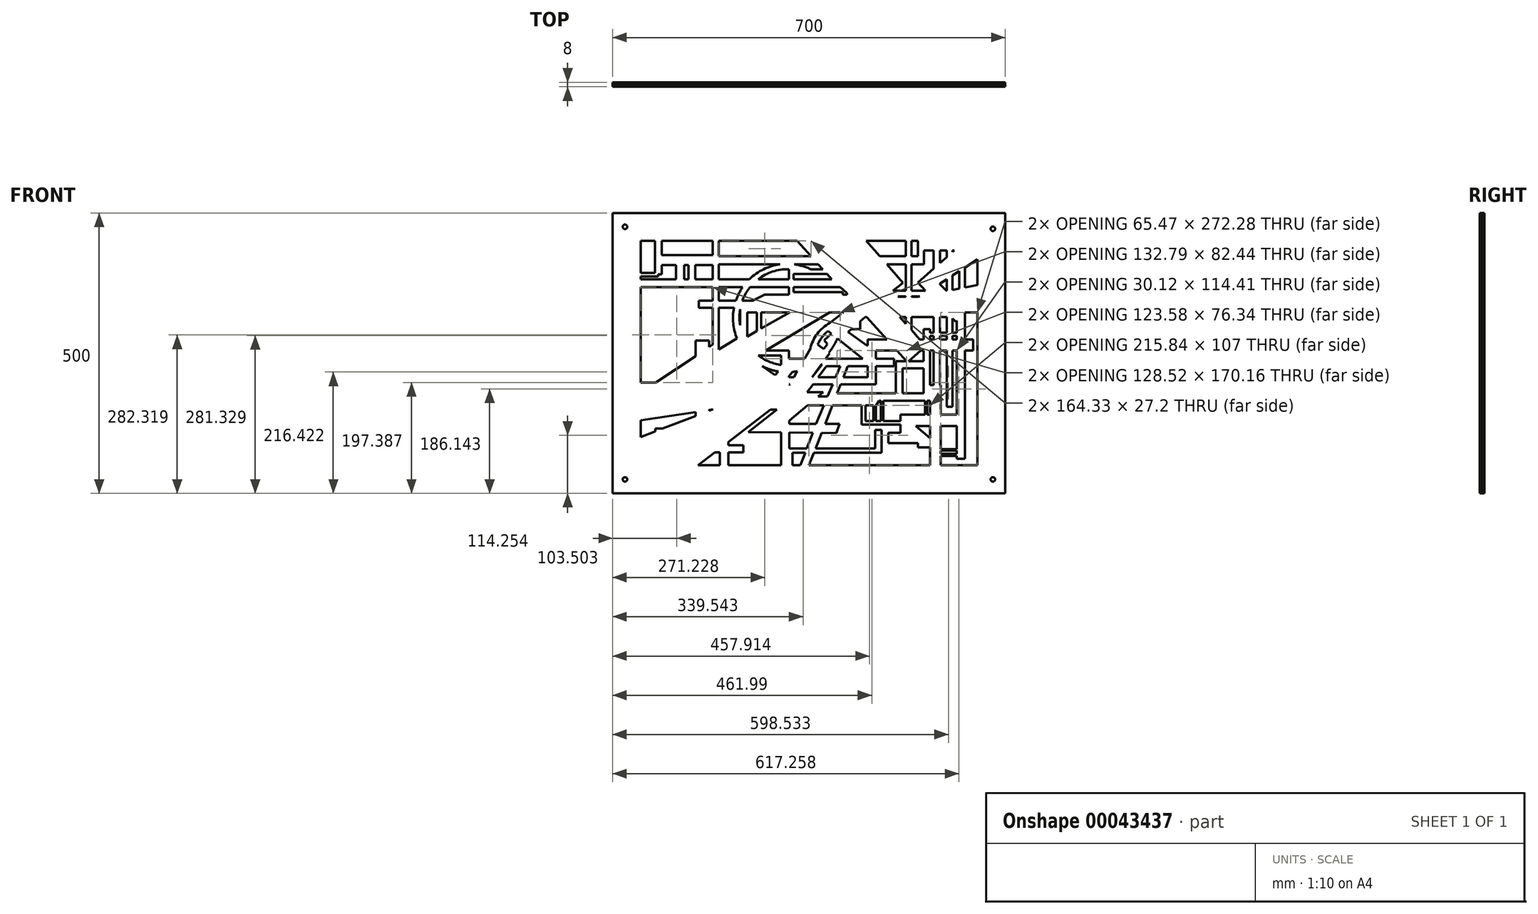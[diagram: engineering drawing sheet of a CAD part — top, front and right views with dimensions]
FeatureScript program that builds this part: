
annotation { "Feature Type Name" : "Feature", "Feature Type Description" : "" }
export const myFeature = defineFeature(function(context is Context, id is Id, definition is map)
    precondition{}
    {
        {
            var Q0;
            Q0=qCreatedBy(makeId("Front.planeOp"),FACE);
            var sketch = newSketch(context, id + "F0", { "sketchPlane" : qUnion([Q0])});
            skLineSegment(sketch, "E0.bottom", {"start": v(-405.94, 245.41) * mm, "end": v(294.06, 245.41) * mm});
            skLineSegment(sketch, "E0.top", {"start": v(-405.94, -254.59) * mm, "end": v(294.06, -254.59) * mm});
            skLineSegment(sketch, "E0.left", {"start": v(-405.94, 245.41) * mm, "end": v(-405.94, -254.59) * mm});
            skLineSegment(sketch, "E0.right", {"start": v(294.06, 245.41) * mm, "end": v(294.06, -254.59) * mm});
            skLineSegment(sketch, "E1.bottom", {"start": v(-355.94, 195.41) * mm, "end": v(-55.94, 195.41) * mm});
            skLineSegment(sketch, "E1.top", {"start": v(-355.94, -204.59) * mm, "end": v(244.06, -204.59) * mm});
            skLineSegment(sketch, "E1.left", {"start": v(-355.94, 195.41) * mm, "end": v(-355.94, -204.59) * mm});
            skLineSegment(sketch, "E1.right", {"start": v(244.06, 195.41) * mm, "end": v(244.06, -204.59) * mm});
            skLineSegment(sketch, "E2", {"start": v(231.3, 195.41) * mm, "end": v(150.42, 122.81) * mm});
            skLineSegment(sketch, "E3", {"start": v(150.42, 122.81) * mm, "end": v(157.7, 114.7) * mm});
            skLineSegment(sketch, "E4", {"start": v(167.3, 121.13) * mm, "end": v(244.06, 172.52) * mm});
            skLineSegment(sketch, "E5", {"start": v(244.06, 172.52) * mm, "end": v(244.06, 195.41) * mm});
            skLineSegment(sketch, "E6", {"start": v(150.42, 122.81) * mm, "end": v(179.6, 90.3) * mm});
            skLineSegment(sketch, "E7", {"start": v(205.45, 61.5) * mm, "end": v(213.96, 69.15) * mm});
            skLineSegment(sketch, "E8", {"start": v(213.96, 69.15) * mm, "end": v(204.55, 79.64) * mm});
            skLineSegment(sketch, "E9", {"start": v(-355.94, -176.1) * mm, "end": v(-156.42, -87.52) * mm});
            skLineSegment(sketch, "E10", {"start": v(-131.37, -87.52) * mm, "end": v(-322.83, -204.59) * mm});
            skLineSegment(sketch, "E11", {"start": v(-322.83, -204.59) * mm, "end": v(-355.94, -204.59) * mm});
            skLineSegment(sketch, "E12", {"start": v(-55.94, 195.41) * mm, "end": v(39.07, 90.3) * mm});
            skLineSegment(sketch, "E13", {"start": v(108.4, 13.58) * mm, "end": v(115.46, 19.96) * mm});
            skLineSegment(sketch, "E14", {"start": v(115.46, 19.96) * mm, "end": v(61.52, 79.64) * mm});
            skLineSegment(sketch, "E15.trimOffspring", {"start": v(-43.13, 195.41) * mm, "end": v(-15.39, 195.41) * mm});
            skLineSegment(sketch, "E16", {"start": v(-15.39, 195.41) * mm, "end": v(66.72, 104.57) * mm});
            skLineSegment(sketch, "E17", {"start": v(95.32, 90.3) * mm, "end": v(96.17, 91.06) * mm});
            skLineSegment(sketch, "E18", {"start": v(96.17, 91.06) * mm, "end": v(83, 105.63) * mm});
            skLineSegment(sketch, "E19", {"start": v(21.81, 195.41) * mm, "end": v(87.2, 123.08) * mm});
            skLineSegment(sketch, "E20", {"start": v(93.99, 115.56) * mm, "end": v(102.37, 123.13) * mm});
            skLineSegment(sketch, "E21", {"start": v(102.37, 123.13) * mm, "end": v(37.03, 195.41) * mm});
            skLineSegment(sketch, "E22", {"start": v(93.99, 115.56) * mm, "end": v(83, 105.63) * mm});
            skLineSegment(sketch, "E23", {"start": v(-21.98, 10.73) * mm, "end": v(-28.78, 18.25) * mm});
            skLineSegment(sketch, "E24", {"start": v(-28.78, 18.25) * mm, "end": v(39.14, 79.64) * mm});
            skLineSegment(sketch, "E25.trimOffspring", {"start": v(76.2, 113.14) * mm, "end": v(1.85, 195.41) * mm});
            skLineSegment(sketch, "E26.trimOffspring", {"start": v(76.2, 113.14) * mm, "end": v(87.2, 123.08) * mm});
            skLineSegment(sketch, "E27.trimOffspring", {"start": v(73.52, 97.05) * mm, "end": v(66.04, 90.3) * mm});
            skLineSegment(sketch, "E28.trimOffspring", {"start": v(73.52, 97.05) * mm, "end": v(79.63, 90.3) * mm});
            skLineSegment(sketch, "E29.trimOffspring", {"start": v(51.45, 90.77) * mm, "end": v(-43.13, 195.41) * mm});
            skLineSegment(sketch, "E30.trimOffspring", {"start": v(51.2, 76.88) * mm, "end": v(-21.98, 10.73) * mm});
            skLineSegment(sketch, "E31.trimOffspring", {"start": v(51.45, 90.77) * mm, "end": v(66.72, 104.57) * mm});
            skLineSegment(sketch, "E32.trimOffspring", {"start": v(51.2, 76.88) * mm, "end": v(108.4, 13.58) * mm});
            skLineSegment(sketch, "E33.trimOffspring", {"start": v(1.85, 195.41) * mm, "end": v(21.81, 195.41) * mm});
            skLineSegment(sketch, "E34.trimOffspring", {"start": v(37.03, 195.41) * mm, "end": v(244.06, 195.41) * mm});
            skLineSegment(sketch, "E35", {"start": v(244.06, 79.64) * mm, "end": v(204.55, 79.64) * mm});
            skLineSegment(sketch, "E36", {"start": v(-158.13, 79.64) * mm, "end": v(-133.99, 90.3) * mm});
            skLineSegment(sketch, "E37", {"start": v(-133.99, 90.3) * mm, "end": v(39.07, 90.3) * mm});
            skLineSegment(sketch, "E38", {"start": v(244.06, 90.3) * mm, "end": v(244.06, 79.64) * mm});
            skLineSegment(sketch, "E39.trimOffspring", {"start": v(95.32, 90.3) * mm, "end": v(179.6, 90.3) * mm});
            skLineSegment(sketch, "E40.trimOffspring", {"start": v(194.99, 90.3) * mm, "end": v(167.3, 121.13) * mm});
            skLineSegment(sketch, "E41.trimOffspring", {"start": v(194.99, 90.3) * mm, "end": v(244.06, 90.3) * mm});
            skLineSegment(sketch, "E42.trimOffspring", {"start": v(189.17, 79.64) * mm, "end": v(205.45, 61.5) * mm});
            skLineSegment(sketch, "E43.trimOffspring", {"start": v(189.17, 79.64) * mm, "end": v(61.52, 79.64) * mm});
            skLineSegment(sketch, "E44.trimOffspring", {"start": v(66.04, 90.3) * mm, "end": v(79.63, 90.3) * mm});
            skLineSegment(sketch, "E45.trimOffspring", {"start": v(39.14, 79.64) * mm, "end": v(-19.56, 79.64) * mm});
            skLineSegment(sketch, "E46", {"start": v(-325.73, -79.87) * mm, "end": v(-46.1, 79.64) * mm});
            skLineSegment(sketch, "E47", {"start": v(-19.56, 79.64) * mm, "end": v(-169.55, -12.55) * mm});
            skLineSegment(sketch, "E48", {"start": v(-257.48, -66.6) * mm, "end": v(-115.3, -66.6) * mm});
            skLineSegment(sketch, "E49", {"start": v(-115.3, -66.6) * mm, "end": v(-185.8, -22.54) * mm});
            skLineSegment(sketch, "E50", {"start": v(-169.55, -12.55) * mm, "end": v(-89.7, -67.55) * mm});
            skLineSegment(sketch, "E51", {"start": v(-89.7, -67.55) * mm, "end": v(-43.18, 0) * mm});
            skLineSegment(sketch, "E52", {"start": v(-43.18, 0) * mm, "end": v(-33.39, -6.75) * mm});
            skLineSegment(sketch, "E53", {"start": v(-33.39, -6.75) * mm, "end": v(-82.64, -78.26) * mm});
            skLineSegment(sketch, "E54", {"start": v(-82.64, -78.26) * mm, "end": v(-131.37, -87.52) * mm});
            skLineSegment(sketch, "E55.trimOffspring", {"start": v(-185.8, -22.54) * mm, "end": v(-257.48, -66.6) * mm});
            skLineSegment(sketch, "E56.trimOffspring", {"start": v(-46.1, 79.64) * mm, "end": v(-158.13, 79.64) * mm});
            skLineSegment(sketch, "E57", {"start": v(-156.42, -87.52) * mm, "end": v(-325.73, -79.87) * mm});
            skCircle(sketch, "E58", {"center": v(-383.92, 220.59) * mm, "radius": 4 * mm});
            skCircle(sketch, "E59", {"center": v(-383.92, -229.76) * mm, "radius": 4 * mm});
            skCircle(sketch, "E60", {"center": v(271.85, -229.76) * mm, "radius": 4 * mm});
            skCircle(sketch, "E61", {"center": v(271.85, 217.02) * mm, "radius": 4 * mm});
            skLineSegment(sketch, "E62", {"start": v(37.03, 195.41) * mm, "end": v(-69.9, 195.41) * mm});
            skSolve(sketch);
        }
        {
            var Q0;
            Q0=makeQuery(id+"F0.imprint","IMPRINT",FACE,{"disambiguationData":[TD([[makeQuery(id+"F0.imprint","IMPRINT",EDGE,{"derivedFrom":sQuery(id+"F0.wireOp",EDGE,"E0.bottom")}),-1.0]])]});
            extrude(context, id + "F1", {"entities" : qUnion([Q0]), "depth" : 4 * mm});
        }
        {
            var Q0;
            Q0=makeQuery(id+"F1.opExtrude","SWEPT_BODY",BODY,{"disambiguationData":[OSD([sQuery(id+"F0.wireOp",EDGE,"E0.bottom"),sQuery(id+"F0.wireOp",EDGE,"E0.top"),sQuery(id+"F0.wireOp",EDGE,"E0.left"),sQuery(id+"F0.wireOp",EDGE,"E0.right"),sQuery(id+"F0.wireOp",EDGE,"E1.bottom"),sQuery(id+"F0.wireOp",EDGE,"E1.top"),sQuery(id+"F0.wireOp",EDGE,"E1.left"),sQuery(id+"F0.wireOp",EDGE,"E1.right"),sQuery(id+"F0.wireOp",EDGE,"E5"),sQuery(id+"F0.wireOp",EDGE,"E11"),sQuery(id+"F0.wireOp",EDGE,"E34.trimOffspring"),sQuery(id+"F0.wireOp",EDGE,"E38"),sQuery(id+"F0.wireOp",EDGE,"E58"),sQuery(id+"F0.wireOp",EDGE,"E59"),sQuery(id+"F0.wireOp",EDGE,"E60"),sQuery(id+"F0.wireOp",EDGE,"E61"),sQuery(id+"F0.wireOp",EDGE,"E62")])]});
            transform(context, id + "F2", {"entities" : qUnion([Q0]), "transformType" : TransformType.COPY});
        }
        {
            var Q0;
            Q0=makeQuery(id+"F1.opExtrude","SWEPT_BODY",BODY,{"disambiguationData":[OSD([sQuery(id+"F0.wireOp",EDGE,"E0.bottom"),sQuery(id+"F0.wireOp",EDGE,"E0.top"),sQuery(id+"F0.wireOp",EDGE,"E0.left"),sQuery(id+"F0.wireOp",EDGE,"E0.right"),sQuery(id+"F0.wireOp",EDGE,"E1.bottom"),sQuery(id+"F0.wireOp",EDGE,"E1.top"),sQuery(id+"F0.wireOp",EDGE,"E1.left"),sQuery(id+"F0.wireOp",EDGE,"E1.right"),sQuery(id+"F0.wireOp",EDGE,"E5"),sQuery(id+"F0.wireOp",EDGE,"E11"),sQuery(id+"F0.wireOp",EDGE,"E34.trimOffspring"),sQuery(id+"F0.wireOp",EDGE,"E38"),sQuery(id+"F0.wireOp",EDGE,"E58"),sQuery(id+"F0.wireOp",EDGE,"E59"),sQuery(id+"F0.wireOp",EDGE,"E60"),sQuery(id+"F0.wireOp",EDGE,"E61"),sQuery(id+"F0.wireOp",EDGE,"E62")])]});
            transform(context, id + "F3", {"entities" : qUnion([Q0]), "transformType" : TransformType.COPY});
        }
        {
            var Q0;
            Q0=makeQuery(id+"F1.opExtrude","SWEPT_BODY",BODY,{"disambiguationData":[OSD([sQuery(id+"F0.wireOp",EDGE,"E0.bottom"),sQuery(id+"F0.wireOp",EDGE,"E0.top"),sQuery(id+"F0.wireOp",EDGE,"E0.left"),sQuery(id+"F0.wireOp",EDGE,"E0.right"),sQuery(id+"F0.wireOp",EDGE,"E1.bottom"),sQuery(id+"F0.wireOp",EDGE,"E1.top"),sQuery(id+"F0.wireOp",EDGE,"E1.left"),sQuery(id+"F0.wireOp",EDGE,"E1.right"),sQuery(id+"F0.wireOp",EDGE,"E5"),sQuery(id+"F0.wireOp",EDGE,"E11"),sQuery(id+"F0.wireOp",EDGE,"E34.trimOffspring"),sQuery(id+"F0.wireOp",EDGE,"E38"),sQuery(id+"F0.wireOp",EDGE,"E58"),sQuery(id+"F0.wireOp",EDGE,"E59"),sQuery(id+"F0.wireOp",EDGE,"E60"),sQuery(id+"F0.wireOp",EDGE,"E61"),sQuery(id+"F0.wireOp",EDGE,"E62")])]});
            transform(context, id + "F4", {"entities" : qUnion([Q0]), "transformType" : TransformType.COPY});
        }
        {
            var Q0;
            Q0=makeQuery(id+"F1.opExtrude","SWEPT_BODY",BODY,{"disambiguationData":[OSD([sQuery(id+"F0.wireOp",EDGE,"E0.bottom"),sQuery(id+"F0.wireOp",EDGE,"E0.top"),sQuery(id+"F0.wireOp",EDGE,"E0.left"),sQuery(id+"F0.wireOp",EDGE,"E0.right"),sQuery(id+"F0.wireOp",EDGE,"E1.bottom"),sQuery(id+"F0.wireOp",EDGE,"E1.top"),sQuery(id+"F0.wireOp",EDGE,"E1.left"),sQuery(id+"F0.wireOp",EDGE,"E1.right"),sQuery(id+"F0.wireOp",EDGE,"E5"),sQuery(id+"F0.wireOp",EDGE,"E11"),sQuery(id+"F0.wireOp",EDGE,"E34.trimOffspring"),sQuery(id+"F0.wireOp",EDGE,"E38"),sQuery(id+"F0.wireOp",EDGE,"E58"),sQuery(id+"F0.wireOp",EDGE,"E59"),sQuery(id+"F0.wireOp",EDGE,"E60"),sQuery(id+"F0.wireOp",EDGE,"E61"),sQuery(id+"F0.wireOp",EDGE,"E62")])]});
            transform(context, id + "F5", {"entities" : qUnion([Q0]), "transformType" : TransformType.COPY});
        }
        {
            var Q0;
            Q0=makeQuery(id+"F1.opExtrude","SWEPT_BODY",BODY,{"disambiguationData":[OSD([sQuery(id+"F0.wireOp",EDGE,"E0.bottom"),sQuery(id+"F0.wireOp",EDGE,"E0.top"),sQuery(id+"F0.wireOp",EDGE,"E0.left"),sQuery(id+"F0.wireOp",EDGE,"E0.right"),sQuery(id+"F0.wireOp",EDGE,"E1.bottom"),sQuery(id+"F0.wireOp",EDGE,"E1.top"),sQuery(id+"F0.wireOp",EDGE,"E1.left"),sQuery(id+"F0.wireOp",EDGE,"E1.right"),sQuery(id+"F0.wireOp",EDGE,"E5"),sQuery(id+"F0.wireOp",EDGE,"E11"),sQuery(id+"F0.wireOp",EDGE,"E34.trimOffspring"),sQuery(id+"F0.wireOp",EDGE,"E38"),sQuery(id+"F0.wireOp",EDGE,"E58"),sQuery(id+"F0.wireOp",EDGE,"E59"),sQuery(id+"F0.wireOp",EDGE,"E60"),sQuery(id+"F0.wireOp",EDGE,"E61"),sQuery(id+"F0.wireOp",EDGE,"E62")])]});
            transform(context, id + "F6", {"entities" : qUnion([Q0]), "transformType" : TransformType.COPY});
        }
        {
            var Q0;
            Q0=makeQuery(id+"F1.opExtrude","SWEPT_BODY",BODY,{"disambiguationData":[OSD([sQuery(id+"F0.wireOp",EDGE,"E0.bottom"),sQuery(id+"F0.wireOp",EDGE,"E0.top"),sQuery(id+"F0.wireOp",EDGE,"E0.left"),sQuery(id+"F0.wireOp",EDGE,"E0.right"),sQuery(id+"F0.wireOp",EDGE,"E1.bottom"),sQuery(id+"F0.wireOp",EDGE,"E1.top"),sQuery(id+"F0.wireOp",EDGE,"E1.left"),sQuery(id+"F0.wireOp",EDGE,"E1.right"),sQuery(id+"F0.wireOp",EDGE,"E5"),sQuery(id+"F0.wireOp",EDGE,"E11"),sQuery(id+"F0.wireOp",EDGE,"E34.trimOffspring"),sQuery(id+"F0.wireOp",EDGE,"E38"),sQuery(id+"F0.wireOp",EDGE,"E58"),sQuery(id+"F0.wireOp",EDGE,"E59"),sQuery(id+"F0.wireOp",EDGE,"E60"),sQuery(id+"F0.wireOp",EDGE,"E61"),sQuery(id+"F0.wireOp",EDGE,"E62")])]});
            transform(context, id + "F7", {"entities" : qUnion([Q0]), "transformType" : TransformType.COPY});
        }
        {
            var Q0;
            Q0=makeQuery(id+"F1.opExtrude","SWEPT_BODY",BODY,{"disambiguationData":[OSD([sQuery(id+"F0.wireOp",EDGE,"E0.bottom"),sQuery(id+"F0.wireOp",EDGE,"E0.top"),sQuery(id+"F0.wireOp",EDGE,"E0.left"),sQuery(id+"F0.wireOp",EDGE,"E0.right"),sQuery(id+"F0.wireOp",EDGE,"E1.bottom"),sQuery(id+"F0.wireOp",EDGE,"E1.top"),sQuery(id+"F0.wireOp",EDGE,"E1.left"),sQuery(id+"F0.wireOp",EDGE,"E1.right"),sQuery(id+"F0.wireOp",EDGE,"E5"),sQuery(id+"F0.wireOp",EDGE,"E11"),sQuery(id+"F0.wireOp",EDGE,"E34.trimOffspring"),sQuery(id+"F0.wireOp",EDGE,"E38"),sQuery(id+"F0.wireOp",EDGE,"E58"),sQuery(id+"F0.wireOp",EDGE,"E59"),sQuery(id+"F0.wireOp",EDGE,"E60"),sQuery(id+"F0.wireOp",EDGE,"E61"),sQuery(id+"F0.wireOp",EDGE,"E62")])]});
            transform(context, id + "F8", {"entities" : qUnion([Q0]), "transformType" : TransformType.COPY});
        }
        {
            var Q0;
            Q0=makeQuery(id+"F1.opExtrude","SWEPT_BODY",BODY,{"disambiguationData":[OSD([sQuery(id+"F0.wireOp",EDGE,"E0.bottom"),sQuery(id+"F0.wireOp",EDGE,"E0.top"),sQuery(id+"F0.wireOp",EDGE,"E0.left"),sQuery(id+"F0.wireOp",EDGE,"E0.right"),sQuery(id+"F0.wireOp",EDGE,"E1.bottom"),sQuery(id+"F0.wireOp",EDGE,"E1.top"),sQuery(id+"F0.wireOp",EDGE,"E1.left"),sQuery(id+"F0.wireOp",EDGE,"E1.right"),sQuery(id+"F0.wireOp",EDGE,"E5"),sQuery(id+"F0.wireOp",EDGE,"E11"),sQuery(id+"F0.wireOp",EDGE,"E34.trimOffspring"),sQuery(id+"F0.wireOp",EDGE,"E38"),sQuery(id+"F0.wireOp",EDGE,"E58"),sQuery(id+"F0.wireOp",EDGE,"E59"),sQuery(id+"F0.wireOp",EDGE,"E60"),sQuery(id+"F0.wireOp",EDGE,"E61"),sQuery(id+"F0.wireOp",EDGE,"E62")])]});
            transform(context, id + "F9", {"entities" : qUnion([Q0]), "transformType" : TransformType.COPY});
        }
        {
            var Q0;
            Q0=makeQuery(id+"F1.opExtrude","SWEPT_BODY",BODY,{"disambiguationData":[OSD([sQuery(id+"F0.wireOp",EDGE,"E0.bottom"),sQuery(id+"F0.wireOp",EDGE,"E0.top"),sQuery(id+"F0.wireOp",EDGE,"E0.left"),sQuery(id+"F0.wireOp",EDGE,"E0.right"),sQuery(id+"F0.wireOp",EDGE,"E1.bottom"),sQuery(id+"F0.wireOp",EDGE,"E1.top"),sQuery(id+"F0.wireOp",EDGE,"E1.left"),sQuery(id+"F0.wireOp",EDGE,"E1.right"),sQuery(id+"F0.wireOp",EDGE,"E5"),sQuery(id+"F0.wireOp",EDGE,"E11"),sQuery(id+"F0.wireOp",EDGE,"E34.trimOffspring"),sQuery(id+"F0.wireOp",EDGE,"E38"),sQuery(id+"F0.wireOp",EDGE,"E58"),sQuery(id+"F0.wireOp",EDGE,"E59"),sQuery(id+"F0.wireOp",EDGE,"E60"),sQuery(id+"F0.wireOp",EDGE,"E61"),sQuery(id+"F0.wireOp",EDGE,"E62")])]});
            transform(context, id + "F10", {"entities" : qUnion([Q0]), "transformType" : TransformType.COPY});
        }
        {
            var Q0;
            Q0=makeQuery(id+"F1.opExtrude","SWEPT_BODY",BODY,{"disambiguationData":[OSD([sQuery(id+"F0.wireOp",EDGE,"E0.bottom"),sQuery(id+"F0.wireOp",EDGE,"E0.top"),sQuery(id+"F0.wireOp",EDGE,"E0.left"),sQuery(id+"F0.wireOp",EDGE,"E0.right"),sQuery(id+"F0.wireOp",EDGE,"E1.bottom"),sQuery(id+"F0.wireOp",EDGE,"E1.top"),sQuery(id+"F0.wireOp",EDGE,"E1.left"),sQuery(id+"F0.wireOp",EDGE,"E1.right"),sQuery(id+"F0.wireOp",EDGE,"E5"),sQuery(id+"F0.wireOp",EDGE,"E11"),sQuery(id+"F0.wireOp",EDGE,"E34.trimOffspring"),sQuery(id+"F0.wireOp",EDGE,"E38"),sQuery(id+"F0.wireOp",EDGE,"E58"),sQuery(id+"F0.wireOp",EDGE,"E59"),sQuery(id+"F0.wireOp",EDGE,"E60"),sQuery(id+"F0.wireOp",EDGE,"E61"),sQuery(id+"F0.wireOp",EDGE,"E62")])]});
            transform(context, id + "F11", {"entities" : qUnion([Q0]), "transformType" : TransformType.COPY});
        }
        {
            var Q0;
            Q0=makeQuery(id+"F1.opExtrude","SWEPT_BODY",BODY,{"disambiguationData":[OSD([sQuery(id+"F0.wireOp",EDGE,"E0.bottom"),sQuery(id+"F0.wireOp",EDGE,"E0.top"),sQuery(id+"F0.wireOp",EDGE,"E0.left"),sQuery(id+"F0.wireOp",EDGE,"E0.right"),sQuery(id+"F0.wireOp",EDGE,"E1.bottom"),sQuery(id+"F0.wireOp",EDGE,"E1.top"),sQuery(id+"F0.wireOp",EDGE,"E1.left"),sQuery(id+"F0.wireOp",EDGE,"E1.right"),sQuery(id+"F0.wireOp",EDGE,"E5"),sQuery(id+"F0.wireOp",EDGE,"E11"),sQuery(id+"F0.wireOp",EDGE,"E34.trimOffspring"),sQuery(id+"F0.wireOp",EDGE,"E38"),sQuery(id+"F0.wireOp",EDGE,"E58"),sQuery(id+"F0.wireOp",EDGE,"E59"),sQuery(id+"F0.wireOp",EDGE,"E60"),sQuery(id+"F0.wireOp",EDGE,"E61"),sQuery(id+"F0.wireOp",EDGE,"E62")])]});
            transform(context, id + "F12", {"entities" : qUnion([Q0]), "transformType" : TransformType.COPY});
        }
        {
            var Q0;
            Q0=makeQuery(id+"F1.opExtrude","SWEPT_BODY",BODY,{"disambiguationData":[OSD([sQuery(id+"F0.wireOp",EDGE,"E0.bottom"),sQuery(id+"F0.wireOp",EDGE,"E0.top"),sQuery(id+"F0.wireOp",EDGE,"E0.left"),sQuery(id+"F0.wireOp",EDGE,"E0.right"),sQuery(id+"F0.wireOp",EDGE,"E1.bottom"),sQuery(id+"F0.wireOp",EDGE,"E1.top"),sQuery(id+"F0.wireOp",EDGE,"E1.left"),sQuery(id+"F0.wireOp",EDGE,"E1.right"),sQuery(id+"F0.wireOp",EDGE,"E5"),sQuery(id+"F0.wireOp",EDGE,"E11"),sQuery(id+"F0.wireOp",EDGE,"E34.trimOffspring"),sQuery(id+"F0.wireOp",EDGE,"E38"),sQuery(id+"F0.wireOp",EDGE,"E58"),sQuery(id+"F0.wireOp",EDGE,"E59"),sQuery(id+"F0.wireOp",EDGE,"E60"),sQuery(id+"F0.wireOp",EDGE,"E61"),sQuery(id+"F0.wireOp",EDGE,"E62")])]});
            transform(context, id + "F13", {"entities" : qUnion([Q0]), "transformType" : TransformType.COPY});
        }
        {
            var Q0;
            Q0=makeQuery(id+"F1.opExtrude","SWEPT_BODY",BODY,{"disambiguationData":[OSD([sQuery(id+"F0.wireOp",EDGE,"E0.bottom"),sQuery(id+"F0.wireOp",EDGE,"E0.top"),sQuery(id+"F0.wireOp",EDGE,"E0.left"),sQuery(id+"F0.wireOp",EDGE,"E0.right"),sQuery(id+"F0.wireOp",EDGE,"E1.bottom"),sQuery(id+"F0.wireOp",EDGE,"E1.top"),sQuery(id+"F0.wireOp",EDGE,"E1.left"),sQuery(id+"F0.wireOp",EDGE,"E1.right"),sQuery(id+"F0.wireOp",EDGE,"E5"),sQuery(id+"F0.wireOp",EDGE,"E11"),sQuery(id+"F0.wireOp",EDGE,"E34.trimOffspring"),sQuery(id+"F0.wireOp",EDGE,"E38"),sQuery(id+"F0.wireOp",EDGE,"E58"),sQuery(id+"F0.wireOp",EDGE,"E59"),sQuery(id+"F0.wireOp",EDGE,"E60"),sQuery(id+"F0.wireOp",EDGE,"E61"),sQuery(id+"F0.wireOp",EDGE,"E62")])]});
            transform(context, id + "F14", {"entities" : qUnion([Q0]), "transformType" : TransformType.COPY});
        }
        {
            var Q0;
            Q0=makeQuery(id+"F1.opExtrude","SWEPT_BODY",BODY,{"disambiguationData":[OSD([sQuery(id+"F0.wireOp",EDGE,"E0.bottom"),sQuery(id+"F0.wireOp",EDGE,"E0.top"),sQuery(id+"F0.wireOp",EDGE,"E0.left"),sQuery(id+"F0.wireOp",EDGE,"E0.right"),sQuery(id+"F0.wireOp",EDGE,"E1.bottom"),sQuery(id+"F0.wireOp",EDGE,"E1.top"),sQuery(id+"F0.wireOp",EDGE,"E1.left"),sQuery(id+"F0.wireOp",EDGE,"E1.right"),sQuery(id+"F0.wireOp",EDGE,"E5"),sQuery(id+"F0.wireOp",EDGE,"E11"),sQuery(id+"F0.wireOp",EDGE,"E34.trimOffspring"),sQuery(id+"F0.wireOp",EDGE,"E38"),sQuery(id+"F0.wireOp",EDGE,"E58"),sQuery(id+"F0.wireOp",EDGE,"E59"),sQuery(id+"F0.wireOp",EDGE,"E60"),sQuery(id+"F0.wireOp",EDGE,"E61"),sQuery(id+"F0.wireOp",EDGE,"E62")])]});
            transform(context, id + "F15", {"entities" : qUnion([Q0]), "transformType" : TransformType.COPY});
        }
        {
            var Q0;
            {var subQ13=sQuery(id+"F0.wireOp",EDGE,"E2");Q0=makeQuery(id+"F0.imprint","IMPRINT",FACE,{"disambiguationData":[TD([[makeQuery(id+"F0.imprint","IMPRINT",EDGE,{"derivedFrom":subQ13}),1.0]])]});}
            extrude(context, id + "F16", {"entities" : qUnion([Q0]), "operationType" : NewBodyOperationType.ADD, "depth" : 4 * mm});
        }
        {
            var Q0;
            Q0=qCreatedBy(makeId("Front.planeOp"),FACE);
            var sketch = newSketch(context, id + "F17", { "sketchPlane" : qUnion([Q0])});
            skLineSegment(sketch, "E63.0", {"start": v(-355.94, 195.41) * mm, "end": v(-55.94, 195.41) * mm});
            skLineSegment(sketch, "E63.1", {"start": v(-355.94, 195.41) * mm, "end": v(-355.94, -204.59) * mm});
            skLineSegment(sketch, "E63.2", {"start": v(-43.13, 195.41) * mm, "end": v(-15.39, 195.41) * mm});
            skLineSegment(sketch, "E63.3", {"start": v(37.03, 195.41) * mm, "end": v(-69.9, 195.41) * mm});
            skLineSegment(sketch, "E63.4", {"start": v(37.03, 195.41) * mm, "end": v(244.06, 195.41) * mm});
            skLineSegment(sketch, "E63.5", {"start": v(244.06, 195.41) * mm, "end": v(244.06, -204.59) * mm});
            skLineSegment(sketch, "E63.6", {"start": v(-355.94, -204.59) * mm, "end": v(244.06, -204.59) * mm});
            skLineSegment(sketch, "E64", {"start": v(-63.2, 195.41) * mm, "end": v(30.8, 93.92) * mm});
            skLineSegment(sketch, "E65", {"start": v(30.8, 93.92) * mm, "end": v(-136.04, 93.92) * mm});
            skLineSegment(sketch, "E66", {"start": v(-136.04, 93.92) * mm, "end": v(-172.77, 76.49) * mm});
            skLineSegment(sketch, "E67", {"start": v(-172.77, 76.49) * mm, "end": v(-59.47, 76.49) * mm});
            skLineSegment(sketch, "E68", {"start": v(-59.47, 76.49) * mm, "end": v(-332.14, -74.16) * mm});
            skLineSegment(sketch, "E69", {"start": v(-332.14, -74.16) * mm, "end": v(-355.94, -74.16) * mm});
            skLineSegment(sketch, "E70", {"start": v(-355.94, -90.97) * mm, "end": v(-180.24, -90.97) * mm});
            skLineSegment(sketch, "E71", {"start": v(-180.24, -90.97) * mm, "end": v(-355.94, -165.05) * mm});
            skLineSegment(sketch, "E72", {"start": v(-355.94, -165.05) * mm, "end": v(-355.94, -204.59) * mm});
            skLineSegment(sketch, "E73", {"start": v(-355.94, -204.59) * mm, "end": v(-294.17, -204.59) * mm});
            skLineSegment(sketch, "E74", {"start": v(-294.17, -204.59) * mm, "end": v(-131.06, -97.2) * mm});
            skLineSegment(sketch, "E75", {"start": v(-131.06, -97.2) * mm, "end": v(-75.04, -86) * mm});
            skLineSegment(sketch, "E76", {"start": v(-75.04, -86) * mm, "end": v(-143.52, -134.55) * mm});
            skLineSegment(sketch, "E77", {"start": v(-143.52, -134.55) * mm, "end": v(-111.77, -134.55) * mm});
            skLineSegment(sketch, "E78", {"start": v(-111.77, -134.55) * mm, "end": v(-47.65, -78.52) * mm});
            skLineSegment(sketch, "E79", {"start": v(-47.65, -78.52) * mm, "end": v(-73.8, -78.52) * mm});
            skLineSegment(sketch, "E80", {"start": v(-73.8, -78.52) * mm, "end": v(-19, -5.06) * mm});
            skLineSegment(sketch, "E81", {"start": v(-19, -5.06) * mm, "end": v(-38.88, 9.75) * mm});
            skLineSegment(sketch, "E82", {"start": v(-38.88, 9.75) * mm, "end": v(-46.4, 16.1) * mm});
            skLineSegment(sketch, "E83", {"start": v(-46.4, 16.1) * mm, "end": v(-90.6, -61.1) * mm});
            skLineSegment(sketch, "E84", {"start": v(-90.6, -61.1) * mm, "end": v(-157.83, -15.02) * mm});
            skLineSegment(sketch, "E85", {"start": v(-157.83, -15.02) * mm, "end": v(-14.65, 70.89) * mm});
            skLineSegment(sketch, "E86", {"start": v(-14.65, 70.89) * mm, "end": v(22.08, 70.89) * mm});
            skLineSegment(sketch, "E87", {"start": v(22.08, 70.89) * mm, "end": v(-19, 39.76) * mm});
            skLineSegment(sketch, "E88", {"start": v(-19, 39.76) * mm, "end": v(39.5, -6.3) * mm});
            skLineSegment(sketch, "E89", {"start": v(39.5, -6.3) * mm, "end": v(44.47, 0) * mm});
            skLineSegment(sketch, "E90", {"start": v(44.47, 0) * mm, "end": v(0, 35.01) * mm});
            skLineSegment(sketch, "E91", {"start": v(0, 35.01) * mm, "end": v(43.24, 74) * mm});
            skLineSegment(sketch, "E92", {"start": v(43.24, 74) * mm, "end": v(109.96, 0) * mm});
            skLineSegment(sketch, "E93", {"start": v(109.96, 0) * mm, "end": v(129.48, 17.6) * mm});
            skLineSegment(sketch, "E94", {"start": v(129.48, 17.6) * mm, "end": v(78.52, 74.13) * mm});
            skLineSegment(sketch, "E95", {"start": v(78.52, 74.13) * mm, "end": v(183.31, 74.13) * mm});
            skLineSegment(sketch, "E96", {"start": v(183.31, 74.13) * mm, "end": v(205.72, 51.59) * mm});
            skLineSegment(sketch, "E97", {"start": v(205.72, 51.59) * mm, "end": v(224.77, 70.52) * mm});
            skLineSegment(sketch, "E98", {"start": v(224.77, 70.52) * mm, "end": v(218.5, 76.81) * mm});
            skLineSegment(sketch, "E99", {"start": v(218.5, 76.81) * mm, "end": v(244.06, 76.81) * mm});
            skLineSegment(sketch, "E100", {"start": v(244.06, 76.81) * mm, "end": v(244.06, 95.79) * mm});
            skLineSegment(sketch, "E101", {"start": v(244.06, 95.79) * mm, "end": v(200.12, 95.79) * mm});
            skLineSegment(sketch, "E102", {"start": v(200.12, 95.79) * mm, "end": v(177.09, 118.82) * mm});
            skLineSegment(sketch, "E103", {"start": v(177.09, 118.82) * mm, "end": v(244.06, 162.4) * mm});
            skLineSegment(sketch, "E104", {"start": v(244.06, 162.4) * mm, "end": v(244.06, 195.41) * mm});
            skLineSegment(sketch, "E105", {"start": v(221.91, 195.41) * mm, "end": v(138.5, 121.31) * mm});
            skLineSegment(sketch, "E106", {"start": v(138.5, 121.31) * mm, "end": v(160.98, 96) * mm});
            skLineSegment(sketch, "E107", {"start": v(160.98, 96) * mm, "end": v(103.63, 96) * mm});
            skLineSegment(sketch, "E108", {"start": v(103.63, 96) * mm, "end": v(92.42, 105.75) * mm});
            skLineSegment(sketch, "E109", {"start": v(92.42, 105.75) * mm, "end": v(111.72, 120.69) * mm});
            skLineSegment(sketch, "E110", {"start": v(111.72, 120.69) * mm, "end": v(46.36, 195.41) * mm});
            skLineSegment(sketch, "E111", {"start": v(46.36, 195.41) * mm, "end": v(-63.2, 195.41) * mm});
            skSolve(sketch);
        }
        {
            var Q0;
            {var subQ3=sQuery(id+"F17.wireOp",EDGE,"E64");Q0=makeQuery(id+"F17.imprint","IMPRINT",FACE,{"disambiguationData":[TD([[makeQuery(id+"F17.imprint","IMPRINT",EDGE,{"derivedFrom":subQ3}),1.0]])]});}
            var Q1;
            Q1=makeQuery(id+"F2.opPattern","COPY",FACE,{"derivedFrom":makeQuery(id+"F1.opExtrude","CAP_FACE",FACE,{"disambiguationData":[OSD([sQuery(id+"F0.wireOp",EDGE,"E0.bottom"),sQuery(id+"F0.wireOp",EDGE,"E0.top"),sQuery(id+"F0.wireOp",EDGE,"E0.left"),sQuery(id+"F0.wireOp",EDGE,"E0.right"),sQuery(id+"F0.wireOp",EDGE,"E1.bottom"),sQuery(id+"F0.wireOp",EDGE,"E1.top"),sQuery(id+"F0.wireOp",EDGE,"E1.left"),sQuery(id+"F0.wireOp",EDGE,"E1.right"),sQuery(id+"F0.wireOp",EDGE,"E5"),sQuery(id+"F0.wireOp",EDGE,"E11"),sQuery(id+"F0.wireOp",EDGE,"E34.trimOffspring"),sQuery(id+"F0.wireOp",EDGE,"E38"),sQuery(id+"F0.wireOp",EDGE,"E58"),sQuery(id+"F0.wireOp",EDGE,"E59"),sQuery(id+"F0.wireOp",EDGE,"E60"),sQuery(id+"F0.wireOp",EDGE,"E61"),sQuery(id+"F0.wireOp",EDGE,"E62")])],"isStart":true}),"instanceName":"1"});
            extrude(context, id + "F18", {"entities" : qUnion([Q0, Q1]), "operationType" : NewBodyOperationType.ADD, "depth" : 4 * mm});
        }
        {
            var Q0;
            Q0=qCreatedBy(makeId("Front.planeOp"),FACE);
            var sketch = newSketch(context, id + "F19", { "sketchPlane" : qUnion([Q0])});
            skLineSegment(sketch, "E112.0", {"start": v(-355.94, 195.41) * mm, "end": v(244.06, 195.41) * mm});
            skLineSegment(sketch, "E112.1", {"start": v(-355.94, 195.41) * mm, "end": v(-355.94, -204.59) * mm});
            skLineSegment(sketch, "E112.2", {"start": v(244.06, -204.59) * mm, "end": v(244.06, 195.41) * mm});
            skLineSegment(sketch, "E112.3", {"start": v(-355.94, -204.59) * mm, "end": v(244.06, -204.59) * mm});
            skLineSegment(sketch, "E113", {"start": v(-77.05, 195.41) * mm, "end": v(-15.71, 127.32) * mm});
            skLineSegment(sketch, "E114", {"start": v(-355.94, 127.32) * mm, "end": v(-15.71, 127.32) * mm});
            skLineSegment(sketch, "E115", {"start": v(-355.94, 127.32) * mm, "end": v(-355.94, 112.81) * mm});
            skLineSegment(sketch, "E116", {"start": v(-355.94, 112.81) * mm, "end": v(0, 112.81) * mm});
            skLineSegment(sketch, "E117", {"start": v(0, 112.81) * mm, "end": v(14.63, 99.62) * mm});
            skLineSegment(sketch, "E118", {"start": v(14.63, 99.62) * mm, "end": v(-135.1, 99.62) * mm});
            skLineSegment(sketch, "E119", {"start": v(-135.1, 99.62) * mm, "end": v(-178.62, 77.85) * mm});
            skLineSegment(sketch, "E120", {"start": v(-178.62, 77.85) * mm, "end": v(-178.62, 25.1) * mm});
            skLineSegment(sketch, "E121", {"start": v(-166.09, 25.1) * mm, "end": v(-166.09, 67.96) * mm});
            skLineSegment(sketch, "E122", {"start": v(-166.09, 67.96) * mm, "end": v(-90.24, 67.96) * mm});
            skLineSegment(sketch, "E123", {"start": v(-90.24, 67.96) * mm, "end": v(-166.09, 25.1) * mm});
            skLineSegment(sketch, "E124", {"start": v(-178.62, 25.1) * mm, "end": v(-328.34, -65.27) * mm});
            skLineSegment(sketch, "E125", {"start": v(-328.34, -65.27) * mm, "end": v(-355.94, -65.27) * mm});
            skLineSegment(sketch, "E126", {"start": v(-355.94, -65.27) * mm, "end": v(-355.94, -104.18) * mm});
            skLineSegment(sketch, "E127", {"start": v(-355.94, -104.18) * mm, "end": v(-203.02, -95.6) * mm});
            skLineSegment(sketch, "E128", {"start": v(-203.02, -95.6) * mm, "end": v(-355.94, -154.3) * mm});
            skLineSegment(sketch, "E129", {"start": v(-355.94, -154.3) * mm, "end": v(-355.94, -204.59) * mm});
            skLineSegment(sketch, "E130", {"start": v(-279.53, -204.59) * mm, "end": v(-132.45, -105.5) * mm});
            skLineSegment(sketch, "E131", {"start": v(-132.45, -105.5) * mm, "end": v(-113.33, -105.5) * mm});
            skLineSegment(sketch, "E132", {"start": v(-113.33, -105.5) * mm, "end": v(-164.11, -145.07) * mm});
            skLineSegment(sketch, "E133", {"start": v(-164.11, -145.07) * mm, "end": v(-49.38, -146.52) * mm});
            skLineSegment(sketch, "E134", {"start": v(-7.14, -147.05) * mm, "end": v(-1.2, -130.56) * mm});
            skLineSegment(sketch, "E135", {"start": v(-1.2, -130.56) * mm, "end": v(-26.97, -130.56) * mm});
            skLineSegment(sketch, "E136", {"start": v(-97.5, -130.56) * mm, "end": v(-30.88, -74.5) * mm});
            skLineSegment(sketch, "E137", {"start": v(-30.88, -74.5) * mm, "end": v(-59.24, -74.5) * mm});
            skLineSegment(sketch, "E138", {"start": v(-59.24, -74.5) * mm, "end": v(-24.95, -27.67) * mm});
            skLineSegment(sketch, "E139", {"start": v(-24.95, -27.67) * mm, "end": v(0, -27.67) * mm});
            skLineSegment(sketch, "E140", {"start": v(0, -27.67) * mm, "end": v(-43.41, -130.56) * mm});
            skLineSegment(sketch, "E141", {"start": v(-49.38, -146.52) * mm, "end": v(-71.11, -204.59) * mm});
            skLineSegment(sketch, "E142", {"start": v(-71.11, -204.59) * mm, "end": v(-55.94, -204.59) * mm});
            skLineSegment(sketch, "E143", {"start": v(-55.94, -204.59) * mm, "end": v(-33.3, -146.72) * mm});
            skLineSegment(sketch, "E144", {"start": v(13.3, -27.67) * mm, "end": v(95.75, -27.67) * mm});
            skLineSegment(sketch, "E145", {"start": v(95.75, -27.67) * mm, "end": v(95.75, -14.48) * mm});
            skLineSegment(sketch, "E146", {"start": v(95.75, -14.48) * mm, "end": v(57.5, -14.48) * mm});
            skLineSegment(sketch, "E147", {"start": v(19.24, -14.48) * mm, "end": v(-15.71, -14.48) * mm});
            skLineSegment(sketch, "E148", {"start": v(-15.71, -14.48) * mm, "end": v(-100.13, -14.48) * mm});
            skLineSegment(sketch, "E149", {"start": v(-100.13, -14.48) * mm, "end": v(-100.13, -25.04) * mm});
            skLineSegment(sketch, "E150", {"start": v(-100.13, -25.04) * mm, "end": v(-32.86, -25.04) * mm});
            skLineSegment(sketch, "E151", {"start": v(-32.86, -25.04) * mm, "end": v(-84.3, -90.99) * mm});
            skLineSegment(sketch, "E152", {"start": v(-84.3, -90.99) * mm, "end": v(-131.13, -90.99) * mm});
            skLineSegment(sketch, "E153", {"start": v(-131.13, -90.99) * mm, "end": v(-73.75, -25.04) * mm});
            skLineSegment(sketch, "E154", {"start": v(-100.13, -25.04) * mm, "end": v(-147.42, -79.38) * mm});
            skLineSegment(sketch, "E155", {"start": v(-147.42, -79.38) * mm, "end": v(-307.9, -79.38) * mm});
            skLineSegment(sketch, "E156", {"start": v(-307.9, -79.38) * mm, "end": v(-52.65, 67.96) * mm});
            skLineSegment(sketch, "E157", {"start": v(-52.65, 67.96) * mm, "end": v(5.4, 67.96) * mm});
            skLineSegment(sketch, "E158", {"start": v(5.4, 67.96) * mm, "end": v(-29.56, 40.92) * mm});
            skLineSegment(sketch, "E159", {"start": v(-29.56, 40.92) * mm, "end": v(39.69, -14.48) * mm});
            skLineSegment(sketch, "E160", {"start": v(57.5, -14.48) * mm, "end": v(57.5, 0) * mm});
            skLineSegment(sketch, "E161", {"start": v(57.5, 0) * mm, "end": v(57.5, 8.6) * mm});
            skLineSegment(sketch, "E162", {"start": v(57.5, 8.6) * mm, "end": v(47.6, 8.6) * mm});
            skLineSegment(sketch, "E163", {"start": v(47.6, 8.6) * mm, "end": v(13.97, 33) * mm});
            skLineSegment(sketch, "E164", {"start": v(13.97, 33) * mm, "end": v(45.63, 61.37) * mm});
            skLineSegment(sketch, "E165", {"start": v(45.63, 61.37) * mm, "end": v(106.18, -6.23) * mm});
            skLineSegment(sketch, "E166", {"start": v(106.18, -6.23) * mm, "end": v(119.5, -21.08) * mm});
            skLineSegment(sketch, "E167", {"start": v(119.5, -21.08) * mm, "end": v(152.12, 8.18) * mm});
            skLineSegment(sketch, "E168", {"start": v(152.12, 8.18) * mm, "end": v(98.75, 67.7) * mm});
            skLineSegment(sketch, "E169", {"start": v(98.75, 67.7) * mm, "end": v(244.06, 67.7) * mm});
            skLineSegment(sketch, "E170", {"start": v(244.06, 67.7) * mm, "end": v(244.06, 116.77) * mm});
            skLineSegment(sketch, "E171", {"start": v(244.06, 116.77) * mm, "end": v(59.48, 80.5) * mm});
            skLineSegment(sketch, "E172", {"start": v(59.48, 80.5) * mm, "end": v(-36.16, 195.41) * mm});
            skLineSegment(sketch, "E173", {"start": v(-36.16, 195.41) * mm, "end": v(-77.05, 195.41) * mm});
            skLineSegment(sketch, "E174.trimOffspring", {"start": v(39.69, -14.48) * mm, "end": v(19.24, -14.48) * mm});
            skLineSegment(sketch, "E175.trimOffspring", {"start": v(-43.41, -130.56) * mm, "end": v(-97.5, -130.56) * mm});
            skLineSegment(sketch, "E176.trimOffspring", {"start": v(-26.97, -130.56) * mm, "end": v(13.3, -27.67) * mm});
            skLineSegment(sketch, "E177.trimOffspring", {"start": v(-33.3, -146.72) * mm, "end": v(-7.14, -147.05) * mm});
            skSolve(sketch);
        }
        {
            var Q0;
            Q0=makeQuery(id+"F19.imprint","IMPRINT",FACE,{"disambiguationData":[TD([[makeQuery(id+"F19.imprint","IMPRINT",EDGE,{"derivedFrom":sQuery(id+"F19.wireOp",EDGE,"E113")}),1.0]])]});
            extrude(context, id + "F20", {"entities" : qUnion([Q0]), "operationType" : NewBodyOperationType.ADD, "depth" : 4 * mm});
        }
        {
            var Q0;
            Q0=qCreatedBy(makeId("Front.planeOp"),FACE);
            var sketch = newSketch(context, id + "F21", { "sketchPlane" : qUnion([Q0])});
            skLineSegment(sketch, "E178.0", {"start": v(-355.94, 195.41) * mm, "end": v(244.06, 195.41) * mm});
            skLineSegment(sketch, "E178.1", {"start": v(-355.94, 195.41) * mm, "end": v(-355.94, -204.59) * mm});
            skLineSegment(sketch, "E178.2", {"start": v(244.06, -204.59) * mm, "end": v(244.06, 195.41) * mm});
            skLineSegment(sketch, "E178.3", {"start": v(-355.94, -204.59) * mm, "end": v(244.06, -204.59) * mm});
            skLineSegment(sketch, "E179", {"start": v(222.38, 195.41) * mm, "end": v(222.38, 19.81) * mm});
            skLineSegment(sketch, "E180", {"start": v(222.38, -122.65) * mm, "end": v(211.83, -122.65) * mm});
            skLineSegment(sketch, "E181", {"start": v(211.83, -122.65) * mm, "end": v(211.83, 0) * mm});
            skLineSegment(sketch, "E182", {"start": v(211.83, 178.77) * mm, "end": v(199.96, 178.77) * mm});
            skLineSegment(sketch, "E183", {"start": v(199.96, 178.77) * mm, "end": v(199.96, 19.81) * mm});
            skLineSegment(sketch, "E184", {"start": v(199.96, -100.22) * mm, "end": v(189.4, -100.22) * mm});
            skLineSegment(sketch, "E185", {"start": v(189.4, -100.22) * mm, "end": v(189.4, 0) * mm});
            skLineSegment(sketch, "E186", {"start": v(189.4, 178.77) * mm, "end": v(177.53, 178.77) * mm});
            skLineSegment(sketch, "E187", {"start": v(177.53, 178.77) * mm, "end": v(177.53, 19.81) * mm});
            skLineSegment(sketch, "E188", {"start": v(177.53, -74.5) * mm, "end": v(166.32, -74.5) * mm});
            skLineSegment(sketch, "E189", {"start": v(166.32, -74.5) * mm, "end": v(166.32, 0) * mm});
            skLineSegment(sketch, "E190", {"start": v(166.32, 178.77) * mm, "end": v(149.17, 178.77) * mm});
            skLineSegment(sketch, "E191", {"start": v(149.17, 178.77) * mm, "end": v(149.17, 153.7) * mm});
            skLineSegment(sketch, "E192", {"start": v(149.17, 153.7) * mm, "end": v(-216.87, 153.7) * mm});
            skLineSegment(sketch, "E193", {"start": v(-251.17, 153.7) * mm, "end": v(-251.17, 168.21) * mm});
            skLineSegment(sketch, "E194", {"start": v(-251.17, 168.21) * mm, "end": v(-227.43, 168.21) * mm});
            skLineSegment(sketch, "E195", {"start": v(137.96, 168.21) * mm, "end": v(137.96, 195.41) * mm});
            skLineSegment(sketch, "E196", {"start": v(137.96, 195.41) * mm, "end": v(222.38, 195.41) * mm});
            skLineSegment(sketch, "E197", {"start": v(-216.87, 195.41) * mm, "end": v(-216.87, -47.46) * mm});
            skLineSegment(sketch, "E198", {"start": v(-216.87, -47.46) * mm, "end": v(48.92, -47.46) * mm});
            skLineSegment(sketch, "E199", {"start": v(48.92, -47.46) * mm, "end": v(48.92, 19.81) * mm});
            skLineSegment(sketch, "E200", {"start": v(48.92, 19.81) * mm, "end": v(166.32, 19.81) * mm});
            skLineSegment(sketch, "E201", {"start": v(236.9, 19.81) * mm, "end": v(236.9, 0) * mm});
            skLineSegment(sketch, "E202", {"start": v(236.9, 0) * mm, "end": v(222.38, 0) * mm});
            skLineSegment(sketch, "E203", {"start": v(63.43, 0) * mm, "end": v(63.43, -60) * mm});
            skLineSegment(sketch, "E204", {"start": v(63.43, -60) * mm, "end": v(-90.9, -60) * mm});
            skLineSegment(sketch, "E205", {"start": v(-90.9, -60) * mm, "end": v(-109.37, -81.76) * mm});
            skLineSegment(sketch, "E206", {"start": v(-109.37, -81.76) * mm, "end": v(73.33, -81.76) * mm});
            skLineSegment(sketch, "E207", {"start": v(73.33, -81.76) * mm, "end": v(64.1, -97.59) * mm});
            skLineSegment(sketch, "E208", {"start": v(64.1, -97.59) * mm, "end": v(-114.64, -97.59) * mm});
            skLineSegment(sketch, "E209", {"start": v(-114.64, -97.59) * mm, "end": v(-253.8, -204.59) * mm});
            skLineSegment(sketch, "E210", {"start": v(-253.8, -204.59) * mm, "end": v(-330.32, -204.59) * mm});
            skLineSegment(sketch, "E211", {"start": v(-330.32, -204.59) * mm, "end": v(-145.64, -97.59) * mm});
            skLineSegment(sketch, "E212", {"start": v(-145.64, -97.59) * mm, "end": v(-145.64, -60) * mm});
            skLineSegment(sketch, "E213", {"start": v(-145.64, -60) * mm, "end": v(-225.45, -60) * mm});
            skLineSegment(sketch, "E214", {"start": v(-225.45, -60) * mm, "end": v(-274.91, -71.2) * mm});
            skLineSegment(sketch, "E215", {"start": v(-274.91, -71.2) * mm, "end": v(-154.88, -71.2) * mm});
            skLineSegment(sketch, "E216", {"start": v(-154.88, -71.2) * mm, "end": v(-154.88, -93.63) * mm});
            skLineSegment(sketch, "E217", {"start": v(-154.88, -93.63) * mm, "end": v(-355.94, -124.63) * mm});
            skLineSegment(sketch, "E218", {"start": v(-355.94, -124.63) * mm, "end": v(-355.94, -57.35) * mm});
            skLineSegment(sketch, "E219", {"start": v(-355.94, -57.35) * mm, "end": v(-329, -57.35) * mm});
            skLineSegment(sketch, "E220", {"start": v(-329, -57.35) * mm, "end": v(-227.43, 10.58) * mm});
            skLineSegment(sketch, "E221", {"start": v(-227.43, 10.58) * mm, "end": v(-227.43, 153.7) * mm});
            skLineSegment(sketch, "E222", {"start": v(-227.43, 168.21) * mm, "end": v(-227.43, 195.41) * mm});
            skLineSegment(sketch, "E223", {"start": v(-227.43, 195.41) * mm, "end": v(-216.87, 195.41) * mm});
            skLineSegment(sketch, "E224.trimOffspring", {"start": v(177.53, 19.81) * mm, "end": v(189.4, 19.81) * mm});
            skLineSegment(sketch, "E225.trimOffspring", {"start": v(166.32, 0) * mm, "end": v(63.43, 0) * mm});
            skLineSegment(sketch, "E226.trimOffspring", {"start": v(199.96, 19.81) * mm, "end": v(211.83, 19.81) * mm});
            skLineSegment(sketch, "E227.trimOffspring", {"start": v(189.4, 0) * mm, "end": v(177.53, 0) * mm});
            skLineSegment(sketch, "E228.trimOffspring", {"start": v(222.38, 19.81) * mm, "end": v(236.9, 19.81) * mm});
            skLineSegment(sketch, "E229.trimOffspring", {"start": v(211.83, 0) * mm, "end": v(199.96, 0) * mm});
            skLineSegment(sketch, "E230.trimOffspring", {"start": v(166.32, 19.81) * mm, "end": v(166.32, 178.77) * mm});
            skLineSegment(sketch, "E231.trimOffspring", {"start": v(177.53, 0) * mm, "end": v(177.53, -74.5) * mm});
            skLineSegment(sketch, "E232.trimOffspring", {"start": v(189.4, 19.81) * mm, "end": v(189.4, 178.77) * mm});
            skLineSegment(sketch, "E233.trimOffspring", {"start": v(199.96, 0) * mm, "end": v(199.96, -100.22) * mm});
            skLineSegment(sketch, "E234.trimOffspring", {"start": v(211.83, 19.81) * mm, "end": v(211.83, 178.77) * mm});
            skLineSegment(sketch, "E235.trimOffspring", {"start": v(222.38, 0) * mm, "end": v(222.38, -122.65) * mm});
            skLineSegment(sketch, "E236.trimOffspring", {"start": v(-227.43, 153.7) * mm, "end": v(-251.17, 153.7) * mm});
            skLineSegment(sketch, "E237.trimOffspring", {"start": v(-216.87, 168.21) * mm, "end": v(137.96, 168.21) * mm});
            skSolve(sketch);
        }
        {
            var Q0;
            Q0=makeQuery(id+"F21.imprint","IMPRINT",FACE,{"disambiguationData":[TD([[makeQuery(id+"F21.imprint","IMPRINT",EDGE,{"derivedFrom":sQuery(id+"F21.wireOp",EDGE,"E179")}),-1.0]])]});
            extrude(context, id + "F22", {"entities" : qUnion([Q0]), "operationType" : NewBodyOperationType.ADD, "depth" : 4 * mm});
        }
        {
            var Q0;
            Q0=makeQuery(id+"F5.opPattern","COPY",FACE,{"derivedFrom":makeQuery(id+"F1.opExtrude","CAP_FACE",FACE,{"disambiguationData":[OSD([sQuery(id+"F0.wireOp",EDGE,"E0.bottom"),sQuery(id+"F0.wireOp",EDGE,"E0.top"),sQuery(id+"F0.wireOp",EDGE,"E0.left"),sQuery(id+"F0.wireOp",EDGE,"E0.right"),sQuery(id+"F0.wireOp",EDGE,"E1.bottom"),sQuery(id+"F0.wireOp",EDGE,"E1.top"),sQuery(id+"F0.wireOp",EDGE,"E1.left"),sQuery(id+"F0.wireOp",EDGE,"E1.right"),sQuery(id+"F0.wireOp",EDGE,"E5"),sQuery(id+"F0.wireOp",EDGE,"E11"),sQuery(id+"F0.wireOp",EDGE,"E34.trimOffspring"),sQuery(id+"F0.wireOp",EDGE,"E38"),sQuery(id+"F0.wireOp",EDGE,"E58"),sQuery(id+"F0.wireOp",EDGE,"E59"),sQuery(id+"F0.wireOp",EDGE,"E60"),sQuery(id+"F0.wireOp",EDGE,"E61"),sQuery(id+"F0.wireOp",EDGE,"E62")])],"isStart":false}),"instanceName":"1"});
            var sketch = newSketch(context, id + "F23", { "sketchPlane" : qUnion([Q0])});
            skLineSegment(sketch, "E238.0", {"start": v(-355.94, 195.41) * mm, "end": v(244.06, 195.41) * mm});
            skLineSegment(sketch, "E238.1", {"start": v(-355.94, 195.41) * mm, "end": v(-355.94, -204.59) * mm});
            skLineSegment(sketch, "E238.2", {"start": v(244.06, -204.59) * mm, "end": v(244.06, 195.41) * mm});
            skLineSegment(sketch, "E238.3", {"start": v(-355.94, -204.59) * mm, "end": v(244.06, -204.59) * mm});
            skLineSegment(sketch, "E239", {"start": v(-330.32, 195.41) * mm, "end": v(-330.32, 135.9) * mm});
            skLineSegment(sketch, "E240", {"start": v(-330.32, 135.9) * mm, "end": v(-318.44, 135.9) * mm});
            skLineSegment(sketch, "E241", {"start": v(-318.44, 135.9) * mm, "end": v(-318.44, 152.38) * mm});
            skLineSegment(sketch, "E242", {"start": v(-318.44, 152.38) * mm, "end": v(-292.72, 152.38) * mm});
            skArc(sketch, "E243", {"start": v(-132.75, 126.3) * mm, "mid": v(-233.44, 120.86) * mm, "end": v(-219.9, 20.93) * mm});
            skArc(sketch, "E244", {"start": v(-166.37, 128.26) * mm, "mid": v(-214.62, 117.85) * mm, "end": v(-233.42, 72.2) * mm});
            skArc(sketch, "E245", {"start": v(244.06, -105.23) * mm, "mid": v(207.47, -85.84) * mm, "end": v(166.1, -84.6) * mm});
            skArc(sketch, "E246", {"start": v(244.06, -127.3) * mm, "mid": v(209.2, -102.31) * mm, "end": v(166.37, -100.16) * mm});
            skArc(sketch, "E247", {"start": v(205.32, -204.59) * mm, "mid": v(215.95, -154.95) * mm, "end": v(167.11, -141.09) * mm});
            skCircle(sketch, "E248", {"center": v(184.13, -174.1) * mm, "radius": 21.6 * mm});
            skLineSegment(sketch, "E249", {"start": v(147, -174.1) * mm, "end": v(108.1, -174.1) * mm});
            skLineSegment(sketch, "E250", {"start": v(148.93, -162.28) * mm, "end": v(109.02, -162.28) * mm});
            skLineSegment(sketch, "E251", {"start": v(147.86, 195.41) * mm, "end": v(148.3, 170.45) * mm});
            skLineSegment(sketch, "E252", {"start": v(161.05, 195.41) * mm, "end": v(161.75, 156.38) * mm});
            skArc(sketch, "E253.trimOffspring", {"start": v(153.26, -104.6) * mm, "mid": v(123.8, -127.82) * mm, "end": v(109.02, -162.28) * mm});
            skArc(sketch, "E254.trimOffspring", {"start": v(152.97, -88.29) * mm, "mid": v(101.57, -135.14) * mm, "end": v(98.09, -204.59) * mm});
            skArc(sketch, "E255.trimOffspring", {"start": v(108.1, -174.1) * mm, "mid": v(109.71, -189.67) * mm, "end": v(114.48, -204.59) * mm});
            skArc(sketch, "E256.trimOffspring", {"start": v(154.12, -152.22) * mm, "mid": v(151.14, -157.05) * mm, "end": v(148.93, -162.28) * mm});
            skArc(sketch, "E257.trimOffspring", {"start": v(147, -174.1) * mm, "mid": v(151.22, -191.3) * mm, "end": v(162.94, -204.59) * mm});
            skLineSegment(sketch, "E258.trimOffspring", {"start": v(166.37, -100.16) * mm, "end": v(167.11, -141.09) * mm});
            skLineSegment(sketch, "E259.trimOffspring", {"start": v(153.26, -104.6) * mm, "end": v(154.12, -152.22) * mm});
            skLineSegment(sketch, "E260", {"start": v(165.55, -54.75) * mm, "end": v(244.06, -53.34) * mm});
            skLineSegment(sketch, "E261", {"start": v(165.25, -37.6) * mm, "end": v(244.06, -36.19) * mm});
            skLineSegment(sketch, "E262", {"start": v(152.36, -54.75) * mm, "end": v(59.48, -162.28) * mm});
            skLineSegment(sketch, "E263", {"start": v(152.05, -37.6) * mm, "end": v(46.94, -153.65) * mm});
            skLineSegment(sketch, "E264", {"start": v(46.94, -153.65) * mm, "end": v(46.94, 0) * mm});
            skLineSegment(sketch, "E265", {"start": v(46.94, 0) * mm, "end": v(151.34, 1.88) * mm});
            skLineSegment(sketch, "E266", {"start": v(150.98, 21.77) * mm, "end": v(46.94, 19.9) * mm});
            skLineSegment(sketch, "E267", {"start": v(46.94, 19.9) * mm, "end": v(2.1, -17.78) * mm});
            skLineSegment(sketch, "E268", {"start": v(2.1, -17.78) * mm, "end": v(29.8, -17.78) * mm});
            skLineSegment(sketch, "E269", {"start": v(29.8, -17.78) * mm, "end": v(29.8, -130.97) * mm});
            skLineSegment(sketch, "E270", {"start": v(29.8, -170.8) * mm, "end": v(79.5, -170.8) * mm});
            skLineSegment(sketch, "E271", {"start": v(79.5, -162.28) * mm, "end": v(59.48, -162.28) * mm});
            skLineSegment(sketch, "E272.trimOffspring", {"start": v(152.36, -54.75) * mm, "end": v(152.97, -88.29) * mm});
            skLineSegment(sketch, "E273.trimOffspring", {"start": v(165.55, -54.75) * mm, "end": v(166.1, -84.6) * mm});
            skLineSegment(sketch, "E274.trimOffspring", {"start": v(151.34, 1.88) * mm, "end": v(152.05, -37.6) * mm});
            skLineSegment(sketch, "E275", {"start": v(-14.02, -17.78) * mm, "end": v(47.59, 34.78) * mm});
            skLineSegment(sketch, "E276", {"start": v(47.59, 34.78) * mm, "end": v(37.27, 46.87) * mm});
            skLineSegment(sketch, "E277", {"start": v(37.27, 46.87) * mm, "end": v(12.7, 25.9) * mm});
            skLineSegment(sketch, "E278", {"start": v(12.7, 25.9) * mm, "end": v(12.7, 126.3) * mm});
            skLineSegment(sketch, "E279", {"start": v(12.7, 126.3) * mm, "end": v(-132.75, 126.3) * mm});
            skLineSegment(sketch, "E280", {"start": v(-119.33, 108.02) * mm, "end": v(0, 108.02) * mm});
            skLineSegment(sketch, "E281", {"start": v(0, 108.02) * mm, "end": v(0, 72.2) * mm});
            skLineSegment(sketch, "E282", {"start": v(0, 19.83) * mm, "end": v(-137.27, -92.87) * mm});
            skLineSegment(sketch, "E283", {"start": v(-137.27, -92.87) * mm, "end": v(-137.27, 23.95) * mm});
            skLineSegment(sketch, "E284", {"start": v(-153.97, 13.92) * mm, "end": v(-153.97, -49.47) * mm});
            skLineSegment(sketch, "E285", {"start": v(-153.97, -204.59) * mm, "end": v(-138.16, -204.59) * mm});
            skLineSegment(sketch, "E286", {"start": v(-138.16, -204.59) * mm, "end": v(-138.16, -114) * mm});
            skLineSegment(sketch, "E287", {"start": v(-138.16, -114) * mm, "end": v(-119.67, -114) * mm});
            skLineSegment(sketch, "E288", {"start": v(-119.67, -114) * mm, "end": v(-119.67, -148.33) * mm});
            skLineSegment(sketch, "E289", {"start": v(-119.67, -148.33) * mm, "end": v(-104.7, -147.45) * mm});
            skLineSegment(sketch, "E290", {"start": v(-104.7, -130.97) * mm, "end": v(-104.7, -102.55) * mm});
            skLineSegment(sketch, "E291", {"start": v(-104.7, -102.55) * mm, "end": v(-31.63, -41.8) * mm});
            skLineSegment(sketch, "E292", {"start": v(-14.02, -17.78) * mm, "end": v(-40.33, -40.6) * mm});
            skLineSegment(sketch, "E293", {"start": v(-40.33, -40.6) * mm, "end": v(-31.63, -41.8) * mm});
            skLineSegment(sketch, "E294", {"start": v(0, 63.92) * mm, "end": v(-113.27, 63.92) * mm});
            skLineSegment(sketch, "E295", {"start": v(0, 72.2) * mm, "end": v(-112.17, 72.2) * mm});
            skLineSegment(sketch, "E296", {"start": v(-152.3, 122.04) * mm, "end": v(-152.3, 72.2) * mm});
            skLineSegment(sketch, "E297", {"start": v(-166.37, 72.2) * mm, "end": v(-166.37, 128.26) * mm});
            skLineSegment(sketch, "E298.trimOffspring", {"start": v(-127.75, 72.2) * mm, "end": v(-152.3, 72.2) * mm});
            skLineSegment(sketch, "E299.trimOffspring", {"start": v(-129.2, 63.92) * mm, "end": v(-159.5, 63.92) * mm});
            skArc(sketch, "E300.trimOffspring", {"start": v(-112.17, 72.2) * mm, "mid": v(-113.32, 90.6) * mm, "end": v(-119.33, 108.02) * mm});
            skArc(sketch, "E301.trimOffspring", {"start": v(-127.75, 72.2) * mm, "mid": v(-132.98, 100.6) * mm, "end": v(-152.3, 122.04) * mm});
            skArc(sketch, "E302.trimOffspring", {"start": v(-231.97, 63.92) * mm, "mid": v(-223.6, 46.08) * mm, "end": v(-209.3, 32.52) * mm});
            skArc(sketch, "E303.trimOffspring", {"start": v(-137.27, 23.95) * mm, "mid": v(-121.77, 41.84) * mm, "end": v(-113.27, 63.92) * mm});
            skLineSegment(sketch, "E304.trimOffspring", {"start": v(0, 63.92) * mm, "end": v(0, 19.83) * mm});
            skLineSegment(sketch, "E305", {"start": v(-159.5, 63.92) * mm, "end": v(-194.12, 25.83) * mm});
            skLineSegment(sketch, "E306", {"start": v(-317.13, -109.46) * mm, "end": v(-329.14, -98.53) * mm});
            skLineSegment(sketch, "E307", {"start": v(-329.14, -98.53) * mm, "end": v(-219.9, 20.93) * mm});
            skLineSegment(sketch, "E308", {"start": v(-263.14, -50.07) * mm, "end": v(-153.97, -109.46) * mm});
            skLineSegment(sketch, "E309", {"start": v(-153.97, -95.33) * mm, "end": v(-255.29, -41.44) * mm});
            skLineSegment(sketch, "E310", {"start": v(-238.3, -22.77) * mm, "end": v(-153.97, -73.2) * mm});
            skLineSegment(sketch, "E311", {"start": v(-153.97, -49.47) * mm, "end": v(-225.74, -8.94) * mm});
            skLineSegment(sketch, "E312.trimOffspring", {"start": v(-238.3, -22.77) * mm, "end": v(-255.29, -41.44) * mm});
            skLineSegment(sketch, "E313.trimOffspring", {"start": v(-153.97, -73.2) * mm, "end": v(-153.97, -95.33) * mm});
            skLineSegment(sketch, "E314.trimOffspring", {"start": v(-153.97, -109.46) * mm, "end": v(-153.97, -204.59) * mm});
            skLineSegment(sketch, "E315.trimOffspring", {"start": v(-263.14, -50.07) * mm, "end": v(-317.13, -109.46) * mm});
            skPoint(sketch, "E316.end.orphan", {"position": v(-230.07, 152.38) * mm});
            skPoint(sketch, "E317.start.orphan", {"position": v(-270.96, 152.38) * mm});
            skLineSegment(sketch, "E318.trimOffspring", {"start": v(-166.37, 72.2) * mm, "end": v(-233.42, 72.2) * mm});
            skLineSegment(sketch, "E319.trimOffspring", {"start": v(-180.58, 63.92) * mm, "end": v(-231.97, 63.92) * mm});
            skLineSegment(sketch, "E320", {"start": v(-104.7, -147.45) * mm, "end": v(29.8, -147.45) * mm});
            skLineSegment(sketch, "E321", {"start": v(30.14, -130.97) * mm, "end": v(-104.7, -130.97) * mm});
            skLineSegment(sketch, "E322.trimOffspring", {"start": v(29.8, -147.45) * mm, "end": v(29.8, -170.8) * mm});
            skArc(sketch, "E323.trimOffspring", {"start": v(-194.12, 25.83) * mm, "mid": v(-153.73, 31.37) * mm, "end": v(-129.2, 63.92) * mm});
            skArc(sketch, "E324.trimOffspring", {"start": v(-205.56, 13.26) * mm, "mid": v(-179.7, 8.55) * mm, "end": v(-153.97, 13.92) * mm});
            skLineSegment(sketch, "E325.trimOffspring", {"start": v(-205.56, 13.26) * mm, "end": v(-225.74, -8.94) * mm});
            skLineSegment(sketch, "E326.trimOffspring", {"start": v(-209.3, 32.52) * mm, "end": v(-180.58, 63.92) * mm});
            skLineSegment(sketch, "E327", {"start": v(-292.72, 152.38) * mm, "end": v(-292.72, -58.7) * mm});
            skLineSegment(sketch, "E328", {"start": v(-292.72, -58.7) * mm, "end": v(-278.59, -43.25) * mm});
            skLineSegment(sketch, "E329", {"start": v(-278.59, -43.25) * mm, "end": v(-278.59, 152.38) * mm});
            skLineSegment(sketch, "E330", {"start": v(-278.59, 152.38) * mm, "end": v(-270.96, 152.38) * mm});
            skLineSegment(sketch, "E331", {"start": v(-270.96, 74.1) * mm, "end": v(-270.96, 152.38) * mm});
            skLineSegment(sketch, "E332", {"start": v(-270.96, 74.1) * mm, "end": v(-258.96, 74.1) * mm});
            skLineSegment(sketch, "E333", {"start": v(-258.96, 74.1) * mm, "end": v(-258.96, 152.38) * mm});
            skLineSegment(sketch, "E334", {"start": v(-258.96, 152.38) * mm, "end": v(-230.07, 152.38) * mm});
            skLineSegment(sketch, "E335", {"start": v(-230.07, 152.38) * mm, "end": v(148.63, 152.38) * mm});
            skLineSegment(sketch, "E336", {"start": v(162.11, 136.2) * mm, "end": v(198.19, 92.9) * mm});
            skLineSegment(sketch, "E337", {"start": v(198.19, 92.9) * mm, "end": v(214.64, 92.9) * mm});
            skLineSegment(sketch, "E338", {"start": v(214.64, 92.9) * mm, "end": v(161.75, 156.38) * mm});
            skLineSegment(sketch, "E339", {"start": v(161.75, 156.38) * mm, "end": v(161.5, 170.45) * mm});
            skLineSegment(sketch, "E340", {"start": v(148.3, 170.45) * mm, "end": v(-318.44, 170.45) * mm});
            skLineSegment(sketch, "E341", {"start": v(-318.44, 170.45) * mm, "end": v(-318.44, 195.41) * mm});
            skLineSegment(sketch, "E342.trimOffspring", {"start": v(148.63, 152.38) * mm, "end": v(150.98, 21.77) * mm});
            skLineSegment(sketch, "E343.trimOffspring", {"start": v(162.11, 136.2) * mm, "end": v(165.25, -37.6) * mm});
            skLineSegment(sketch, "E344", {"start": v(79.5, -170.8) * mm, "end": v(79.5, -162.28) * mm});
            skPoint(sketch, "E345.end.orphan", {"position": v(92.9, -162.28) * mm});
            skSolve(sketch);
        }
        {
            var Q0;
            {var subQ14=sQuery(id+"F23.wireOp",EDGE,"E239");Q0=makeQuery(id+"F23.imprint","IMPRINT",FACE,{"disambiguationData":[TD([[makeQuery(id+"F23.imprint","IMPRINT",EDGE,{"derivedFrom":subQ14}),1.0]])]});}
            extrude(context, id + "F24", {"entities" : qUnion([Q0]), "operationType" : NewBodyOperationType.ADD, "oppositeDirection" : true, "depth" : 4 * mm});
        }
        {
            var Q0;
            Q0=makeQuery(id+"F6.opPattern","COPY",FACE,{"derivedFrom":makeQuery(id+"F1.opExtrude","CAP_FACE",FACE,{"disambiguationData":[OSD([sQuery(id+"F0.wireOp",EDGE,"E0.bottom"),sQuery(id+"F0.wireOp",EDGE,"E0.top"),sQuery(id+"F0.wireOp",EDGE,"E0.left"),sQuery(id+"F0.wireOp",EDGE,"E0.right"),sQuery(id+"F0.wireOp",EDGE,"E1.bottom"),sQuery(id+"F0.wireOp",EDGE,"E1.top"),sQuery(id+"F0.wireOp",EDGE,"E1.left"),sQuery(id+"F0.wireOp",EDGE,"E1.right"),sQuery(id+"F0.wireOp",EDGE,"E5"),sQuery(id+"F0.wireOp",EDGE,"E11"),sQuery(id+"F0.wireOp",EDGE,"E34.trimOffspring"),sQuery(id+"F0.wireOp",EDGE,"E38"),sQuery(id+"F0.wireOp",EDGE,"E58"),sQuery(id+"F0.wireOp",EDGE,"E59"),sQuery(id+"F0.wireOp",EDGE,"E60"),sQuery(id+"F0.wireOp",EDGE,"E61"),sQuery(id+"F0.wireOp",EDGE,"E62")])],"isStart":true}),"instanceName":"1"});
            var sketch = newSketch(context, id + "F25", { "sketchPlane" : qUnion([Q0])});
            skLineSegment(sketch, "E346.0", {"start": v(355.94, 195.41) * mm, "end": v(-244.06, 195.41) * mm});
            skLineSegment(sketch, "E346.1", {"start": v(-244.06, -204.59) * mm, "end": v(-244.06, 195.41) * mm});
            skLineSegment(sketch, "E346.2", {"start": v(355.94, 195.41) * mm, "end": v(355.94, -204.59) * mm});
            skLineSegment(sketch, "E346.3", {"start": v(355.94, -204.59) * mm, "end": v(-244.06, -204.59) * mm});
            skLineSegment(sketch, "E347", {"start": v(-174.56, 195.41) * mm, "end": v(-174.56, 160.96) * mm});
            skLineSegment(sketch, "E348", {"start": v(-174.56, 160.96) * mm, "end": v(-234.92, 89.07) * mm});
            skLineSegment(sketch, "E349", {"start": v(-234.92, 89.07) * mm, "end": v(-234.92, 66.64) * mm});
            skLineSegment(sketch, "E350", {"start": v(-234.92, 66.64) * mm, "end": v(-185.95, 66.64) * mm});
            skLineSegment(sketch, "E351", {"start": v(-89.16, 66.64) * mm, "end": v(-89.16, -59.33) * mm});
            skLineSegment(sketch, "E352", {"start": v(-89.16, -59.33) * mm, "end": v(0, -182) * mm});
            skLineSegment(sketch, "E353", {"start": v(0, -182) * mm, "end": v(301.96, -182) * mm});
            skLineSegment(sketch, "E354", {"start": v(301.96, -182) * mm, "end": v(301.96, -109.46) * mm});
            skLineSegment(sketch, "E355", {"start": v(301.96, -109.46) * mm, "end": v(288.77, -109.46) * mm});
            skLineSegment(sketch, "E356", {"start": v(288.77, -109.46) * mm, "end": v(288.77, -166.84) * mm});
            skLineSegment(sketch, "E357", {"start": v(288.77, -166.84) * mm, "end": v(276.23, -166.84) * mm});
            skLineSegment(sketch, "E358", {"start": v(12.41, -166.84) * mm, "end": v(-65.41, -59.33) * mm});
            skLineSegment(sketch, "E359", {"start": v(-65.41, -59.33) * mm, "end": v(-65.41, 66.64) * mm});
            skLineSegment(sketch, "E360", {"start": v(-65.41, 66.64) * mm, "end": v(-65.41, 85.1) * mm});
            skLineSegment(sketch, "E361", {"start": v(-65.41, 85.1) * mm, "end": v(72.43, 85.1) * mm});
            skLineSegment(sketch, "E362", {"start": v(98.82, 85.1) * mm, "end": v(98.82, 96.98) * mm});
            skLineSegment(sketch, "E363", {"start": v(98.82, 96.98) * mm, "end": v(73.75, 96.98) * mm});
            skLineSegment(sketch, "E364", {"start": v(-65.41, 96.98) * mm, "end": v(-89.16, 78.51) * mm});
            skLineSegment(sketch, "E365", {"start": v(-89.16, 78.51) * mm, "end": v(-223.04, 78.51) * mm});
            skLineSegment(sketch, "E366", {"start": v(-223.04, 78.51) * mm, "end": v(-223.04, 87.75) * mm});
            skLineSegment(sketch, "E367", {"start": v(-223.04, 87.75) * mm, "end": v(-162.37, 160.96) * mm});
            skLineSegment(sketch, "E368", {"start": v(-162.37, 160.96) * mm, "end": v(-162.37, 195.41) * mm});
            skLineSegment(sketch, "E369", {"start": v(276.23, -166.84) * mm, "end": v(276.23, -47.46) * mm});
            skLineSegment(sketch, "E370", {"start": v(276.23, 0) * mm, "end": v(264.36, 0) * mm});
            skLineSegment(sketch, "E371", {"start": v(264.36, 0) * mm, "end": v(264.36, -36.25) * mm});
            skLineSegment(sketch, "E372.trimOffspring", {"start": v(264.36, -166.84) * mm, "end": v(12.41, -166.84) * mm});
            skLineSegment(sketch, "E373", {"start": v(355.94, -47.46) * mm, "end": v(276.23, -47.46) * mm});
            skLineSegment(sketch, "E374", {"start": v(11.1, -47.46) * mm, "end": v(11.1, -36.25) * mm});
            skLineSegment(sketch, "E375", {"start": v(28.82, -36.25) * mm, "end": v(60.65, -36.25) * mm});
            skLineSegment(sketch, "E376.trimOffspring", {"start": v(276.23, -36.25) * mm, "end": v(355.94, -36.25) * mm});
            skLineSegment(sketch, "E377.trimOffspring", {"start": v(276.23, -36.25) * mm, "end": v(276.23, 0) * mm});
            skLineSegment(sketch, "E378.trimOffspring", {"start": v(264.36, -47.46) * mm, "end": v(264.36, -166.84) * mm});
            skLineSegment(sketch, "E379.trimOffspring", {"start": v(264.36, -47.46) * mm, "end": v(11.1, -47.46) * mm});
            skLineSegment(sketch, "E380", {"start": v(-110.57, 66.64) * mm, "end": v(-110.57, -27.65) * mm});
            skLineSegment(sketch, "E381", {"start": v(-110.57, -27.65) * mm, "end": v(-118.95, -27.65) * mm});
            skLineSegment(sketch, "E382", {"start": v(-118.95, -27.65) * mm, "end": v(-118.95, -7.76) * mm});
            skLineSegment(sketch, "E383", {"start": v(-118.95, 66.64) * mm, "end": v(-127.85, 66.64) * mm});
            skLineSegment(sketch, "E384", {"start": v(-127.85, 66.64) * mm, "end": v(-127.85, 7.42) * mm});
            skLineSegment(sketch, "E385", {"start": v(-127.85, 7.42) * mm, "end": v(-118.95, 7.42) * mm});
            skLineSegment(sketch, "E386", {"start": v(-118.95, -7.76) * mm, "end": v(-185.95, -7.76) * mm});
            skLineSegment(sketch, "E387", {"start": v(-185.95, -7.76) * mm, "end": v(-185.95, 66.64) * mm});
            skLineSegment(sketch, "E388", {"start": v(-170.25, 66.64) * mm, "end": v(-170.25, 7.42) * mm});
            skLineSegment(sketch, "E389", {"start": v(-170.25, 7.42) * mm, "end": v(-136.22, 7.42) * mm});
            skLineSegment(sketch, "E390", {"start": v(-136.22, 7.42) * mm, "end": v(-136.22, 66.64) * mm});
            skLineSegment(sketch, "E391.trimOffspring", {"start": v(-170.25, 66.64) * mm, "end": v(-136.22, 66.64) * mm});
            skLineSegment(sketch, "E392.trimOffspring", {"start": v(-127.85, 66.64) * mm, "end": v(-118.95, 66.64) * mm});
            skLineSegment(sketch, "E393.trimOffspring", {"start": v(-110.57, 66.64) * mm, "end": v(-89.16, 66.64) * mm});
            skLineSegment(sketch, "E394.trimOffspring", {"start": v(-118.95, 7.42) * mm, "end": v(-118.95, 66.64) * mm});
            skLineSegment(sketch, "E395", {"start": v(11.1, -36.25) * mm, "end": v(76.94, 18.55) * mm});
            skLineSegment(sketch, "E396", {"start": v(76.94, 18.55) * mm, "end": v(92.49, 18.55) * mm});
            skLineSegment(sketch, "E397", {"start": v(92.49, 18.55) * mm, "end": v(28.82, -36.25) * mm});
            skLineSegment(sketch, "E398", {"start": v(60.65, -36.25) * mm, "end": v(102.11, 0) * mm});
            skLineSegment(sketch, "E399", {"start": v(102.11, 0) * mm, "end": v(117.66, 0) * mm});
            skLineSegment(sketch, "E400", {"start": v(117.66, 0) * mm, "end": v(76.2, -36.25) * mm});
            skLineSegment(sketch, "E401.trimOffspring", {"start": v(76.2, -36.25) * mm, "end": v(264.36, -36.25) * mm});
            skLineSegment(sketch, "E402", {"start": v(355.94, 39.24) * mm, "end": v(294.85, 39.24) * mm});
            skLineSegment(sketch, "E403", {"start": v(294.85, 39.24) * mm, "end": v(294.85, 105.85) * mm});
            skLineSegment(sketch, "E404", {"start": v(294.85, 195.41) * mm, "end": v(306.68, 195.41) * mm});
            skLineSegment(sketch, "E405", {"start": v(306.68, 195.41) * mm, "end": v(306.68, 119.55) * mm});
            skLineSegment(sketch, "E406", {"start": v(306.68, 54.18) * mm, "end": v(355.94, 54.18) * mm});
            skLineSegment(sketch, "E407", {"start": v(355.94, 54.18) * mm, "end": v(355.94, 105.85) * mm});
            skLineSegment(sketch, "E408", {"start": v(355.94, 105.85) * mm, "end": v(306.68, 105.85) * mm});
            skLineSegment(sketch, "E409", {"start": v(243.18, 105.85) * mm, "end": v(243.18, 119.55) * mm});
            skLineSegment(sketch, "E410", {"start": v(243.18, 119.55) * mm, "end": v(294.85, 119.55) * mm});
            skLineSegment(sketch, "E411", {"start": v(355.94, 119.55) * mm, "end": v(355.94, 132) * mm});
            skLineSegment(sketch, "E412", {"start": v(355.94, 132) * mm, "end": v(324.74, 132) * mm});
            skLineSegment(sketch, "E413", {"start": v(324.74, 132) * mm, "end": v(324.74, 138.64) * mm});
            skLineSegment(sketch, "E414", {"start": v(324.74, 138.64) * mm, "end": v(355.94, 138.64) * mm});
            skLineSegment(sketch, "E415.trimOffspring", {"start": v(306.68, 105.85) * mm, "end": v(306.68, 54.18) * mm});
            skLineSegment(sketch, "E416.trimOffspring", {"start": v(306.68, 119.55) * mm, "end": v(355.94, 119.55) * mm});
            skLineSegment(sketch, "E417.trimOffspring", {"start": v(294.85, 119.55) * mm, "end": v(294.85, 146.2) * mm});
            skLineSegment(sketch, "E418.trimOffspring", {"start": v(294.85, 105.85) * mm, "end": v(243.18, 105.85) * mm});
            skLineSegment(sketch, "E419", {"start": v(65.18, 96.98) * mm, "end": v(65.18, 105.68) * mm});
            skLineSegment(sketch, "E420", {"start": v(65.18, 195.41) * mm, "end": v(73.75, 195.41) * mm});
            skLineSegment(sketch, "E421", {"start": v(73.75, 195.41) * mm, "end": v(73.75, 157.48) * mm});
            skLineSegment(sketch, "E422", {"start": v(85.32, 85.1) * mm, "end": v(124.54, 44.88) * mm});
            skLineSegment(sketch, "E423", {"start": v(124.54, 44.88) * mm, "end": v(112, 44.88) * mm});
            skLineSegment(sketch, "E424", {"start": v(112, 44.88) * mm, "end": v(72.43, 85.1) * mm});
            skLineSegment(sketch, "E425.trimOffspring", {"start": v(65.18, 96.98) * mm, "end": v(-65.41, 96.98) * mm});
            skLineSegment(sketch, "E426.trimOffspring", {"start": v(85.32, 85.1) * mm, "end": v(98.82, 85.1) * mm});
            skLineSegment(sketch, "E427", {"start": v(73.75, 146.2) * mm, "end": v(294.85, 146.2) * mm});
            skLineSegment(sketch, "E428.trimOffspring", {"start": v(294.85, 157.48) * mm, "end": v(294.85, 195.41) * mm});
            skLineSegment(sketch, "E429.trimOffspring", {"start": v(73.75, 146.2) * mm, "end": v(73.75, 118.23) * mm});
            skLineSegment(sketch, "E430", {"start": v(35.4, 195.41) * mm, "end": v(35.4, 118.23) * mm});
            skLineSegment(sketch, "E431", {"start": v(35.4, 118.23) * mm, "end": v(65.18, 118.23) * mm});
            skLineSegment(sketch, "E432", {"start": v(199.34, 118.23) * mm, "end": v(199.34, 105.68) * mm});
            skLineSegment(sketch, "E433", {"start": v(199.34, 105.68) * mm, "end": v(73.75, 105.68) * mm});
            skLineSegment(sketch, "E434", {"start": v(22.07, 105.68) * mm, "end": v(22.07, 195.41) * mm});
            skLineSegment(sketch, "E435", {"start": v(22.07, 195.41) * mm, "end": v(200.12, 195.41) * mm});
            skLineSegment(sketch, "E436", {"start": v(200.12, 195.41) * mm, "end": v(200.12, 157.48) * mm});
            skLineSegment(sketch, "E437", {"start": v(218.16, 157.48) * mm, "end": v(218.16, 195.41) * mm});
            skLineSegment(sketch, "E438.trimOffspring", {"start": v(73.75, 118.23) * mm, "end": v(199.34, 118.23) * mm});
            skLineSegment(sketch, "E439.trimOffspring", {"start": v(65.18, 118.23) * mm, "end": v(65.18, 195.41) * mm});
            skLineSegment(sketch, "E440.trimOffspring", {"start": v(73.75, 105.68) * mm, "end": v(73.75, 96.98) * mm});
            skLineSegment(sketch, "E441.trimOffspring", {"start": v(65.18, 105.68) * mm, "end": v(22.07, 105.68) * mm});
            skLineSegment(sketch, "E442.trimOffspring", {"start": v(200.12, 157.48) * mm, "end": v(73.75, 157.48) * mm});
            skLineSegment(sketch, "E443", {"start": v(218.16, 157.48) * mm, "end": v(294.85, 157.48) * mm});
            skSolve(sketch);
        }
        {
            var Q0;
            {var subQ13=sQuery(id+"F25.wireOp",EDGE,"E347");Q0=makeQuery(id+"F25.imprint","IMPRINT",FACE,{"disambiguationData":[TD([[makeQuery(id+"F25.imprint","IMPRINT",EDGE,{"derivedFrom":subQ13}),1.0]])]});}
            var Q1;
            {var subQ1=sQuery(id+"F25.wireOp",EDGE,"E412");Q1=makeQuery(id+"F25.imprint","IMPRINT",FACE,{"disambiguationData":[TD([[makeQuery(id+"F25.imprint","IMPRINT",EDGE,{"derivedFrom":subQ1}),-1.0]])]});}
            extrude(context, id + "F26", {"entities" : qUnion([Q0, Q1]), "operationType" : NewBodyOperationType.ADD, "oppositeDirection" : true, "depth" : 4 * mm});
        }
        {
            var Q0;
            Q0=qCreatedBy(makeId("Front.planeOp"),FACE);
            var sketch = newSketch(context, id + "F27", { "sketchPlane" : qUnion([Q0])});
            skLineSegment(sketch, "E444.0", {"start": v(-355.94, 195.41) * mm, "end": v(244.06, 195.41) * mm});
            skLineSegment(sketch, "E444.1", {"start": v(-355.94, 195.41) * mm, "end": v(-355.94, -204.59) * mm});
            skLineSegment(sketch, "E444.2", {"start": v(244.06, -204.59) * mm, "end": v(244.06, 195.41) * mm});
            skLineSegment(sketch, "E444.3", {"start": v(-355.94, -204.59) * mm, "end": v(244.06, -204.59) * mm});
            skLineSegment(sketch, "E445", {"start": v(178.58, -204.59) * mm, "end": v(178.58, -187.73) * mm});
            skLineSegment(sketch, "E446", {"start": v(159.9, -156.49) * mm, "end": v(134.28, -134.48) * mm});
            skLineSegment(sketch, "E447", {"start": v(134.28, -134.48) * mm, "end": v(159.9, -134.48) * mm});
            skLineSegment(sketch, "E448", {"start": v(207.65, -114.4) * mm, "end": v(178.58, -114.4) * mm});
            skLineSegment(sketch, "E449", {"start": v(107.29, -114.4) * mm, "end": v(107.29, -125.96) * mm});
            skLineSegment(sketch, "E450", {"start": v(107.29, -146.94) * mm, "end": v(85.83, -146.94) * mm});
            skLineSegment(sketch, "E451", {"start": v(85.83, -146.94) * mm, "end": v(85.83, -164.93) * mm});
            skLineSegment(sketch, "E452", {"start": v(85.83, -164.93) * mm, "end": v(138.43, -164.93) * mm});
            skLineSegment(sketch, "E453", {"start": v(138.43, -164.93) * mm, "end": v(138.43, -172.55) * mm});
            skLineSegment(sketch, "E454", {"start": v(138.43, -172.55) * mm, "end": v(159.9, -172.55) * mm});
            skLineSegment(sketch, "E455", {"start": v(159.9, -172.55) * mm, "end": v(159.9, -204.59) * mm});
            skLineSegment(sketch, "E456", {"start": v(159.9, -204.59) * mm, "end": v(159.9, -172.55) * mm});
            skLineSegment(sketch, "E457", {"start": v(159.9, -61.8) * mm, "end": v(178.58, -61.8) * mm});
            skLineSegment(sketch, "E458", {"start": v(178.58, -61.8) * mm, "end": v(178.58, -114.4) * mm});
            skLineSegment(sketch, "E459.trimOffspring", {"start": v(159.9, -114.4) * mm, "end": v(159.9, -89.49) * mm});
            skLineSegment(sketch, "E460.trimOffspring", {"start": v(159.9, -114.4) * mm, "end": v(154.85, -114.4) * mm});
            skLineSegment(sketch, "E461.trimOffspring", {"start": v(159.9, -156.49) * mm, "end": v(159.9, -134.48) * mm});
            skLineSegment(sketch, "E462", {"start": v(178.58, -134.48) * mm, "end": v(178.58, -172.55) * mm});
            skLineSegment(sketch, "E463.trimOffspring", {"start": v(178.58, -134.48) * mm, "end": v(207.65, -134.48) * mm});
            skLineSegment(sketch, "E464", {"start": v(148.13, -76.34) * mm, "end": v(110.75, -76.34) * mm});
            skLineSegment(sketch, "E465", {"start": v(-18, -76.34) * mm, "end": v(-18, -89.49) * mm});
            skLineSegment(sketch, "E466", {"start": v(-18, -89.49) * mm, "end": v(37.92, -89.49) * mm});
            skLineSegment(sketch, "E467", {"start": v(159.9, 37.87) * mm, "end": v(148.13, 37.87) * mm});
            skLineSegment(sketch, "E468", {"start": v(148.13, 37.87) * mm, "end": v(148.13, 8.86) * mm});
            skLineSegment(sketch, "E469.trimOffspring", {"start": v(159.9, -61.8) * mm, "end": v(159.9, 25.86) * mm});
            skLineSegment(sketch, "E470", {"start": v(-355.94, -181.55) * mm, "end": v(-214.7, -181.55) * mm});
            skLineSegment(sketch, "E471", {"start": v(-173.04, -181.55) * mm, "end": v(-173.04, -169.09) * mm});
            skLineSegment(sketch, "E472", {"start": v(-173.04, -169.09) * mm, "end": v(-199.81, -169.09) * mm});
            skLineSegment(sketch, "E473", {"start": v(-316.32, -169.09) * mm, "end": v(-316.32, -147.63) * mm});
            skLineSegment(sketch, "E474", {"start": v(-316.32, -147.63) * mm, "end": v(-252.64, -147.63) * mm});
            skLineSegment(sketch, "E475", {"start": v(-252.64, -147.63) * mm, "end": v(-252.64, -169.09) * mm});
            skLineSegment(sketch, "E476", {"start": v(-233.95, -169.09) * mm, "end": v(-233.95, -91.98) * mm});
            skLineSegment(sketch, "E477", {"start": v(-233.95, 17.8) * mm, "end": v(-258.18, 17.8) * mm});
            skLineSegment(sketch, "E478", {"start": v(-258.18, 17.8) * mm, "end": v(-258.18, -86.93) * mm});
            skLineSegment(sketch, "E479", {"start": v(-258.18, -139.32) * mm, "end": v(-329.47, -139.32) * mm});
            skLineSegment(sketch, "E480.trimOffspring", {"start": v(-252.64, -169.09) * mm, "end": v(-316.32, -169.09) * mm});
            skLineSegment(sketch, "E481", {"start": v(110.75, -76.34) * mm, "end": v(110.75, -32.04) * mm});
            skLineSegment(sketch, "E482", {"start": v(110.75, -32.04) * mm, "end": v(148.13, -32.04) * mm});
            skLineSegment(sketch, "E483", {"start": v(148.13, -19.23) * mm, "end": v(98.98, -19.23) * mm});
            skLineSegment(sketch, "E484", {"start": v(98.98, -19.23) * mm, "end": v(98.98, -76.34) * mm});
            skLineSegment(sketch, "E485.trimOffspring", {"start": v(148.13, -32.04) * mm, "end": v(148.13, -76.34) * mm});
            skLineSegment(sketch, "E486.trimOffspring", {"start": v(98.98, -76.34) * mm, "end": v(-18, -76.34) * mm});
            skArc(sketch, "E487", {"start": v(-91.9, -38.58) * mm, "mid": v(-32.92, -16.17) * mm, "end": v(-0.36, 37.89) * mm});
            skArc(sketch, "E488", {"start": v(-91.9, -26.36) * mm, "mid": v(-73.24, -23.8) * mm, "end": v(-55.57, -17.23) * mm});
            skArc(sketch, "E489", {"start": v(-10.2, 41.92) * mm, "mid": v(-35.1, 20.34) * mm, "end": v(-45.17, -11.03) * mm});
            skArc(sketch, "E490", {"start": v(-8.58, 53.93) * mm, "mid": v(-43.83, 26.1) * mm, "end": v(-55.57, -17.23) * mm});
            skLineSegment(sketch, "E491", {"start": v(19.31, 76.21) * mm, "end": v(71.53, 76.21) * mm});
            skLineSegment(sketch, "E492", {"start": v(222.19, 76.21) * mm, "end": v(222.19, -193.31) * mm});
            skLineSegment(sketch, "E493", {"start": v(222.19, -193.31) * mm, "end": v(207.65, -193.31) * mm});
            skLineSegment(sketch, "E494", {"start": v(207.65, -193.31) * mm, "end": v(207.65, -187.73) * mm});
            skLineSegment(sketch, "E495", {"start": v(207.65, -114.4) * mm, "end": v(207.65, 25.86) * mm});
            skLineSegment(sketch, "E496", {"start": v(207.65, 60.02) * mm, "end": v(126.56, 60.02) * mm});
            skLineSegment(sketch, "E497", {"start": v(11.88, 76.21) * mm, "end": v(11.88, 60.02) * mm});
            skPoint(sketch, "E498.end.orphan", {"position": v(0, 76.21) * mm});
            skPoint(sketch, "E499.trimOffspring.end.orphan", {"position": v(0, 60.02) * mm});
            skLineSegment(sketch, "E500", {"start": v(37.92, -89.49) * mm, "end": v(37.92, -131.98) * mm});
            skLineSegment(sketch, "E501", {"start": v(37.92, -131.98) * mm, "end": v(107.29, -131.98) * mm});
            skLineSegment(sketch, "E502", {"start": v(107.29, -125.96) * mm, "end": v(76.38, -125.96) * mm});
            skLineSegment(sketch, "E503", {"start": v(44.91, -125.96) * mm, "end": v(44.91, -89.49) * mm});
            skLineSegment(sketch, "E504.trimOffspring", {"start": v(107.29, -131.98) * mm, "end": v(107.29, -146.94) * mm});
            skLineSegment(sketch, "E505.trimOffspring", {"start": v(44.91, -89.49) * mm, "end": v(59.1, -89.49) * mm});
            skLineSegment(sketch, "E506", {"start": v(59.1, -89.49) * mm, "end": v(59.1, -125.96) * mm});
            skLineSegment(sketch, "E507", {"start": v(63.37, -125.96) * mm, "end": v(63.37, -89.49) * mm});
            skLineSegment(sketch, "E508.trimOffspring", {"start": v(63.37, -89.49) * mm, "end": v(71.91, -89.49) * mm});
            skLineSegment(sketch, "E509.trimOffspring", {"start": v(59.1, -125.96) * mm, "end": v(44.91, -125.96) * mm});
            skLineSegment(sketch, "E510", {"start": v(71.91, -89.49) * mm, "end": v(71.91, -125.96) * mm});
            skLineSegment(sketch, "E511", {"start": v(76.38, -125.96) * mm, "end": v(76.38, -89.49) * mm});
            skLineSegment(sketch, "E512.trimOffspring", {"start": v(76.38, -89.49) * mm, "end": v(150.77, -89.49) * mm});
            skLineSegment(sketch, "E513.trimOffspring", {"start": v(71.91, -125.96) * mm, "end": v(63.37, -125.96) * mm});
            skLineSegment(sketch, "E514", {"start": v(154.85, -114.4) * mm, "end": v(154.85, -89.49) * mm});
            skLineSegment(sketch, "E515", {"start": v(150.77, -89.49) * mm, "end": v(150.77, -114.4) * mm});
            skLineSegment(sketch, "E516.trimOffspring", {"start": v(150.77, -114.4) * mm, "end": v(107.29, -114.4) * mm});
            skLineSegment(sketch, "E517.trimOffspring", {"start": v(154.85, -89.49) * mm, "end": v(159.9, -89.49) * mm});
            skLineSegment(sketch, "E518", {"start": v(207.65, -187.73) * mm, "end": v(178.58, -187.73) * mm});
            skLineSegment(sketch, "E519", {"start": v(178.58, -184.23) * mm, "end": v(207.65, -184.23) * mm});
            skLineSegment(sketch, "E520.trimOffspring", {"start": v(207.65, -184.23) * mm, "end": v(207.65, -178.4) * mm});
            skLineSegment(sketch, "E521.trimOffspring", {"start": v(178.58, -184.23) * mm, "end": v(178.58, -178.4) * mm});
            skLineSegment(sketch, "E522", {"start": v(207.65, -178.4) * mm, "end": v(178.58, -178.4) * mm});
            skLineSegment(sketch, "E523", {"start": v(178.58, -175.88) * mm, "end": v(207.65, -175.88) * mm});
            skLineSegment(sketch, "E524.trimOffspring", {"start": v(207.65, -175.88) * mm, "end": v(207.65, -134.48) * mm});
            skLineSegment(sketch, "E525.trimOffspring", {"start": v(178.58, -175.88) * mm, "end": v(178.58, -172.55) * mm});
            skLineSegment(sketch, "E526", {"start": v(-233.95, -8.58) * mm, "end": v(-164.83, -8.58) * mm});
            skLineSegment(sketch, "E527", {"start": v(-105.3, -8.58) * mm, "end": v(-105.3, -25.66) * mm});
            skLineSegment(sketch, "E528", {"start": v(-105.3, -63.29) * mm, "end": v(-91.9, -63.29) * mm});
            skLineSegment(sketch, "E529", {"start": v(-91.9, -63.29) * mm, "end": v(-91.9, -38.58) * mm});
            skLineSegment(sketch, "E530", {"start": v(-91.9, 0) * mm, "end": v(-141.32, 0) * mm});
            skLineSegment(sketch, "E531.trimOffspring", {"start": v(-91.9, -26.36) * mm, "end": v(-91.9, 0) * mm});
            skLineSegment(sketch, "E532.trimOffspring", {"start": v(-105.3, -38.06) * mm, "end": v(-105.3, -63.29) * mm});
            skArc(sketch, "E533.trimOffspring", {"start": v(-146.45, -8.58) * mm, "mid": v(-127, -19.84) * mm, "end": v(-105.3, -25.66) * mm});
            skArc(sketch, "E534.trimOffspring", {"start": v(-164.83, -8.58) * mm, "mid": v(-137.68, -28.6) * mm, "end": v(-105.3, -38.06) * mm});
            skLineSegment(sketch, "E535.trimOffspring", {"start": v(-172.08, 0) * mm, "end": v(-233.95, 0) * mm});
            skLineSegment(sketch, "E536.trimOffspring", {"start": v(-146.45, -8.58) * mm, "end": v(-105.3, -8.58) * mm});
            skArc(sketch, "E537.trimOffspring", {"start": v(-45.17, -11.03) * mm, "mid": v(-22.6, 12.1) * mm, "end": v(-10.2, 41.92) * mm});
            skLineSegment(sketch, "E538.trimOffspring", {"start": v(-233.95, 0) * mm, "end": v(-233.95, 17.8) * mm});
            skLineSegment(sketch, "E539", {"start": v(-329.47, -139.32) * mm, "end": v(-329.47, -169.09) * mm});
            skLineSegment(sketch, "E540", {"start": v(-329.47, -169.09) * mm, "end": v(-355.94, -169.09) * mm});
            skLineSegment(sketch, "E541", {"start": v(-91.9, 145.02) * mm, "end": v(-91.9, 88.88) * mm});
            skLineSegment(sketch, "E542", {"start": v(-91.9, 88.88) * mm, "end": v(-174.6, 88.88) * mm});
            skLineSegment(sketch, "E543", {"start": v(-252.48, 88.88) * mm, "end": v(-252.48, 76.08) * mm});
            skLineSegment(sketch, "E544", {"start": v(-252.48, 76.08) * mm, "end": v(-189.68, 76.08) * mm});
            skLineSegment(sketch, "E545", {"start": v(-83.68, 76.08) * mm, "end": v(-83.68, 95.38) * mm});
            skArc(sketch, "E546.trimOffspring", {"start": v(-178.2, 76.08) * mm, "mid": v(-176.42, 35.32) * mm, "end": v(-156, 0) * mm});
            skArc(sketch, "E547.trimOffspring", {"start": v(-189.68, 76.08) * mm, "mid": v(-188.9, 36.18) * mm, "end": v(-172.08, 0) * mm});
            skLineSegment(sketch, "E548.trimOffspring", {"start": v(-186.3, 88.88) * mm, "end": v(-252.48, 88.88) * mm});
            skLineSegment(sketch, "E549.trimOffspring", {"start": v(-178.2, 76.08) * mm, "end": v(-148.9, 76.08) * mm});
            skArc(sketch, "E550.trimOffspring", {"start": v(-91.9, 145.02) * mm, "mid": v(-142.28, 130.25) * mm, "end": v(-174.6, 88.88) * mm});
            skLineSegment(sketch, "E551", {"start": v(-141.32, 0) * mm, "end": v(-141.32, 76.08) * mm});
            skLineSegment(sketch, "E552", {"start": v(-148.9, 76.08) * mm, "end": v(-148.9, 0) * mm});
            skLineSegment(sketch, "E553.trimOffspring", {"start": v(-148.9, 0) * mm, "end": v(-156, 0) * mm});
            skPoint(sketch, "E554.start.orphan", {"position": v(-147.44, 0) * mm});
            skLineSegment(sketch, "E555.trimOffspring", {"start": v(-141.32, 76.08) * mm, "end": v(-83.68, 76.08) * mm});
            skLineSegment(sketch, "E556", {"start": v(-52.06, 144.53) * mm, "end": v(78.13, 145.02) * mm});
            skLineSegment(sketch, "E557", {"start": v(78.13, 145.02) * mm, "end": v(78.13, 106.73) * mm});
            skLineSegment(sketch, "E558", {"start": v(71.53, 76.21) * mm, "end": v(71.53, 136.52) * mm});
            skLineSegment(sketch, "E559", {"start": v(71.53, 136.52) * mm, "end": v(19.31, 136.52) * mm});
            skArc(sketch, "E560.trimOffspring", {"start": v(-52.06, 144.53) * mm, "mid": v(-131.8, 147.15) * mm, "end": v(-186.3, 88.88) * mm});
            skLineSegment(sketch, "E561", {"start": v(-8.58, 53.93) * mm, "end": v(0, 53.93) * mm});
            skLineSegment(sketch, "E562", {"start": v(28.63, 53.93) * mm, "end": v(28.63, 60.02) * mm});
            skLineSegment(sketch, "E563", {"start": v(35.23, 60.02) * mm, "end": v(35.23, 37.89) * mm});
            skLineSegment(sketch, "E564", {"start": v(35.23, 37.89) * mm, "end": v(-0.36, 37.89) * mm});
            skLineSegment(sketch, "E565.trimOffspring", {"start": v(28.63, 60.02) * mm, "end": v(11.88, 60.02) * mm});
            skLineSegment(sketch, "E566.trimOffspring", {"start": v(78.13, 76.21) * mm, "end": v(116.67, 76.21) * mm});
            skLineSegment(sketch, "E567", {"start": v(78.13, 96.63) * mm, "end": v(116.67, 96.63) * mm});
            skLineSegment(sketch, "E568", {"start": v(244.06, 96.63) * mm, "end": v(244.06, 106.73) * mm});
            skLineSegment(sketch, "E569", {"start": v(244.06, 106.73) * mm, "end": v(126.56, 106.73) * mm});
            skLineSegment(sketch, "E570.trimOffspring", {"start": v(78.13, 96.63) * mm, "end": v(78.13, 76.21) * mm});
            skLineSegment(sketch, "E571", {"start": v(148.13, 0) * mm, "end": v(116.67, 0) * mm});
            skLineSegment(sketch, "E572", {"start": v(116.67, 0) * mm, "end": v(116.67, 60.02) * mm});
            skLineSegment(sketch, "E573", {"start": v(116.67, 195.41) * mm, "end": v(126.56, 195.41) * mm});
            skLineSegment(sketch, "E574", {"start": v(126.56, 195.41) * mm, "end": v(126.56, 106.73) * mm});
            skLineSegment(sketch, "E575", {"start": v(126.56, 8.86) * mm, "end": v(148.13, 8.86) * mm});
            skLineSegment(sketch, "E576.trimOffspring", {"start": v(116.67, 106.73) * mm, "end": v(78.13, 106.73) * mm});
            skLineSegment(sketch, "E577.trimOffspring", {"start": v(126.56, 96.63) * mm, "end": v(126.56, 76.21) * mm});
            skLineSegment(sketch, "E578.trimOffspring", {"start": v(116.67, 106.73) * mm, "end": v(116.67, 195.41) * mm});
            skLineSegment(sketch, "E579.trimOffspring", {"start": v(126.56, 96.63) * mm, "end": v(244.06, 96.63) * mm});
            skLineSegment(sketch, "E580.trimOffspring", {"start": v(126.56, 76.21) * mm, "end": v(222.19, 76.21) * mm});
            skLineSegment(sketch, "E581.trimOffspring", {"start": v(126.56, 60.02) * mm, "end": v(126.56, 8.86) * mm});
            skLineSegment(sketch, "E582.trimOffspring", {"start": v(116.67, 76.21) * mm, "end": v(116.67, 96.63) * mm});
            skLineSegment(sketch, "E583.trimOffspring", {"start": v(148.13, 0) * mm, "end": v(148.13, -19.23) * mm});
            skLineSegment(sketch, "E584.trimOffspring", {"start": v(116.67, 60.02) * mm, "end": v(35.23, 60.02) * mm});
            skLineSegment(sketch, "E585", {"start": v(159.9, 31.74) * mm, "end": v(207.65, 31.74) * mm});
            skLineSegment(sketch, "E586", {"start": v(207.65, 25.86) * mm, "end": v(159.9, 25.86) * mm});
            skLineSegment(sketch, "E587.trimOffspring", {"start": v(159.9, 31.74) * mm, "end": v(159.9, 37.87) * mm});
            skLineSegment(sketch, "E588.trimOffspring", {"start": v(207.65, 31.74) * mm, "end": v(207.65, 60.02) * mm});
            skLineSegment(sketch, "E589", {"start": v(11.88, 76.21) * mm, "end": v(11.88, 136.52) * mm});
            skLineSegment(sketch, "E590", {"start": v(19.31, 136.52) * mm, "end": v(19.31, 76.21) * mm});
            skLineSegment(sketch, "E591.trimOffspring", {"start": v(11.88, 136.52) * mm, "end": v(-83.68, 136.52) * mm});
            skLineSegment(sketch, "E592", {"start": v(-83.68, 95.38) * mm, "end": v(0, 95.38) * mm});
            skLineSegment(sketch, "E593", {"start": v(0, 95.38) * mm, "end": v(0, 53.93) * mm});
            skLineSegment(sketch, "E594", {"start": v(4.52, 53.93) * mm, "end": v(4.52, 103.92) * mm});
            skLineSegment(sketch, "E595", {"start": v(4.52, 103.92) * mm, "end": v(-83.68, 103.92) * mm});
            skLineSegment(sketch, "E596.trimOffspring", {"start": v(-83.68, 103.92) * mm, "end": v(-83.68, 136.52) * mm});
            skLineSegment(sketch, "E597.trimOffspring", {"start": v(4.52, 53.93) * mm, "end": v(28.63, 53.93) * mm});
            skLineSegment(sketch, "E598", {"start": v(-355.94, -91.98) * mm, "end": v(-258.18, -91.98) * mm});
            skLineSegment(sketch, "E599", {"start": v(-258.18, -86.93) * mm, "end": v(-355.94, -86.93) * mm});
            skLineSegment(sketch, "E600.trimOffspring", {"start": v(-258.18, -91.98) * mm, "end": v(-258.18, -139.32) * mm});
            skLineSegment(sketch, "E601", {"start": v(-233.95, -91.98) * mm, "end": v(-214.7, -91.98) * mm});
            skPoint(sketch, "E601.startSnap0", {"position": v(-233.95, -88.83) * mm});
            skLineSegment(sketch, "E602", {"start": v(-214.7, -91.98) * mm, "end": v(-214.7, -169.09) * mm});
            skLineSegment(sketch, "E603", {"start": v(-214.7, -181.55) * mm, "end": v(-214.7, -204.59) * mm});
            skLineSegment(sketch, "E604", {"start": v(-214.7, -204.59) * mm, "end": v(-199.81, -204.59) * mm});
            skLineSegment(sketch, "E605", {"start": v(-199.81, -204.59) * mm, "end": v(-199.81, -181.55) * mm});
            skLineSegment(sketch, "E606", {"start": v(-199.81, -86.93) * mm, "end": v(-233.95, -86.93) * mm});
            skLineSegment(sketch, "E607.trimOffspring", {"start": v(-233.95, -86.93) * mm, "end": v(-233.95, -8.58) * mm});
            skLineSegment(sketch, "E608.trimOffspring", {"start": v(-214.7, -169.09) * mm, "end": v(-233.95, -169.09) * mm});
            skLineSegment(sketch, "E609.trimOffspring", {"start": v(-199.81, -169.09) * mm, "end": v(-199.81, -100.65) * mm});
            skLineSegment(sketch, "E610.trimOffspring", {"start": v(-199.81, -181.55) * mm, "end": v(-173.04, -181.55) * mm});
            skLineSegment(sketch, "E611", {"start": v(-105.3, -74.28) * mm, "end": v(-105.3, -94.47) * mm});
            skLineSegment(sketch, "E612", {"start": v(-105.3, -204.59) * mm, "end": v(-85.4, -204.59) * mm});
            skLineSegment(sketch, "E613", {"start": v(-85.4, -204.59) * mm, "end": v(-85.4, -182.08) * mm});
            skLineSegment(sketch, "E614", {"start": v(-85.4, -182.08) * mm, "end": v(73.37, -182.08) * mm});
            skLineSegment(sketch, "E615", {"start": v(73.37, -182.08) * mm, "end": v(73.37, -141.58) * mm});
            skLineSegment(sketch, "E616", {"start": v(73.37, -141.58) * mm, "end": v(62.26, -141.58) * mm});
            skLineSegment(sketch, "E617", {"start": v(62.26, -141.58) * mm, "end": v(62.26, -174.9) * mm});
            skLineSegment(sketch, "E618", {"start": v(62.26, -174.9) * mm, "end": v(-91.27, -174.9) * mm});
            skLineSegment(sketch, "E619", {"start": v(-91.27, -174.9) * mm, "end": v(-91.27, -74.28) * mm});
            skLineSegment(sketch, "E620", {"start": v(-91.27, -74.28) * mm, "end": v(-105.3, -74.28) * mm});
            skLineSegment(sketch, "E621", {"start": v(-105.3, -94.47) * mm, "end": v(-199.81, -94.47) * mm});
            skLineSegment(sketch, "E622", {"start": v(-199.81, -100.65) * mm, "end": v(-105.3, -100.65) * mm});
            skLineSegment(sketch, "E623.trimOffspring", {"start": v(-105.3, -100.65) * mm, "end": v(-105.3, -204.59) * mm});
            skLineSegment(sketch, "E624.trimOffspring", {"start": v(-199.81, -94.47) * mm, "end": v(-199.81, -86.93) * mm});
            skSolve(sketch);
        }
        {
            var Q0;
            {var subQ5=sQuery(id+"F27.wireOp",EDGE,"E445");Q0=makeQuery(id+"F27.imprint","IMPRINT",FACE,{"disambiguationData":[TD([[makeQuery(id+"F27.imprint","IMPRINT",EDGE,{"derivedFrom":subQ5}),1.0]])]});}
            extrude(context, id + "F28", {"entities" : qUnion([Q0]), "operationType" : NewBodyOperationType.ADD, "depth" : 4 * mm});
        }
        {
            var Q0;
            Q0=makeQuery(id+"F18.boolean.opBoolean","MERGE",FACE,{"derivedFrom":[makeQuery(id+"F2.opPattern","COPY",FACE,{"derivedFrom":makeQuery(id+"F1.opExtrude","CAP_FACE",FACE,{"disambiguationData":[OSD([sQuery(id+"F0.wireOp",EDGE,"E0.bottom"),sQuery(id+"F0.wireOp",EDGE,"E0.top"),sQuery(id+"F0.wireOp",EDGE,"E0.left"),sQuery(id+"F0.wireOp",EDGE,"E0.right"),sQuery(id+"F0.wireOp",EDGE,"E1.bottom"),sQuery(id+"F0.wireOp",EDGE,"E1.top"),sQuery(id+"F0.wireOp",EDGE,"E1.left"),sQuery(id+"F0.wireOp",EDGE,"E1.right"),sQuery(id+"F0.wireOp",EDGE,"E5"),sQuery(id+"F0.wireOp",EDGE,"E11"),sQuery(id+"F0.wireOp",EDGE,"E34.trimOffspring"),sQuery(id+"F0.wireOp",EDGE,"E38"),sQuery(id+"F0.wireOp",EDGE,"E58"),sQuery(id+"F0.wireOp",EDGE,"E59"),sQuery(id+"F0.wireOp",EDGE,"E60"),sQuery(id+"F0.wireOp",EDGE,"E61"),sQuery(id+"F0.wireOp",EDGE,"E62")])],"isStart":true}),"instanceName":"1"}),makeQuery(id+"F18.opExtrude","CAP_FACE",FACE,{"disambiguationData":[OSD([sQuery(id+"F17.wireOp",EDGE,"E63.1"),sQuery(id+"F17.wireOp",EDGE,"E63.4"),sQuery(id+"F17.wireOp",EDGE,"E64"),sQuery(id+"F17.wireOp",EDGE,"E65"),sQuery(id+"F17.wireOp",EDGE,"E66"),sQuery(id+"F17.wireOp",EDGE,"E67"),sQuery(id+"F17.wireOp",EDGE,"E68"),sQuery(id+"F17.wireOp",EDGE,"E69"),sQuery(id+"F17.wireOp",EDGE,"E70"),sQuery(id+"F17.wireOp",EDGE,"E71"),sQuery(id+"F17.wireOp",EDGE,"E72"),sQuery(id+"F17.wireOp",EDGE,"E73"),sQuery(id+"F17.wireOp",EDGE,"E74"),sQuery(id+"F17.wireOp",EDGE,"E75"),sQuery(id+"F17.wireOp",EDGE,"E76"),sQuery(id+"F17.wireOp",EDGE,"E77"),sQuery(id+"F17.wireOp",EDGE,"E78"),sQuery(id+"F17.wireOp",EDGE,"E79"),sQuery(id+"F17.wireOp",EDGE,"E80"),sQuery(id+"F17.wireOp",EDGE,"E81"),sQuery(id+"F17.wireOp",EDGE,"E82"),sQuery(id+"F17.wireOp",EDGE,"E83"),sQuery(id+"F17.wireOp",EDGE,"E84"),sQuery(id+"F17.wireOp",EDGE,"E85"),sQuery(id+"F17.wireOp",EDGE,"E86"),sQuery(id+"F17.wireOp",EDGE,"E87"),sQuery(id+"F17.wireOp",EDGE,"E88"),sQuery(id+"F17.wireOp",EDGE,"E89"),sQuery(id+"F17.wireOp",EDGE,"E90"),sQuery(id+"F17.wireOp",EDGE,"E91"),sQuery(id+"F17.wireOp",EDGE,"E92"),sQuery(id+"F17.wireOp",EDGE,"E93"),sQuery(id+"F17.wireOp",EDGE,"E94"),sQuery(id+"F17.wireOp",EDGE,"E95"),sQuery(id+"F17.wireOp",EDGE,"E96"),sQuery(id+"F17.wireOp",EDGE,"E97"),sQuery(id+"F17.wireOp",EDGE,"E98"),sQuery(id+"F17.wireOp",EDGE,"E99"),sQuery(id+"F17.wireOp",EDGE,"E100"),sQuery(id+"F17.wireOp",EDGE,"E101"),sQuery(id+"F17.wireOp",EDGE,"E102"),sQuery(id+"F17.wireOp",EDGE,"E103"),sQuery(id+"F17.wireOp",EDGE,"E104"),sQuery(id+"F17.wireOp",EDGE,"E105"),sQuery(id+"F17.wireOp",EDGE,"E106"),sQuery(id+"F17.wireOp",EDGE,"E107"),sQuery(id+"F17.wireOp",EDGE,"E108"),sQuery(id+"F17.wireOp",EDGE,"E109"),sQuery(id+"F17.wireOp",EDGE,"E110"),sQuery(id+"F17.wireOp",EDGE,"E111")])],"isStart":true})]});
            extrude(context, id + "F29", {"entities" : qUnion([Q0]), "depth" : 4 * mm});
        }
    });
